# Revit family: 879-002X99-001-DN300-600
name_source: partatom
category: Pipe Accessories
units: mm (PartAtom-declared; Revit-internal decimal feet)

## family parameters
Always vertical = Yes
Cut with Voids When Loaded = No
Part Type = Valve - Breaks Into
Round Connector Dimension = Use Diameter
Shared = No
Work Plane-Based = No

## types (56) — shared parameters
879-0300-00-14400209999 = DN300_PN16
879-0300-00-144002099A0 = DN300_PN16
879-0300-00-14400219999 = DN300_PN16
879-0300-00-144002199A0 = DN300_PN16
879-0300-00-14400229999 = DN300_PN16
879-0300-00-144002299A0 = DN300_PN16
879-0300-00-14400239990 = DN300_PN16
879-0300-00-144002399A0 = DN300_PN16
879-0350-00-14400209999 = DN350_PN16
879-0350-00-144002099A0 = DN350_PN16
879-0350-00-14400219999 = DN350_PN16
879-0350-00-144002199A0 = DN350_PN16
879-0350-00-14400229999 = DN350_PN16
879-0350-00-144002299A0 = DN350_PN16
879-0350-00-14400239999 = DN350_PN16
879-0350-00-144002399A0 = DN350_PN16
879-0400-00-14400209999 = DN400_PN16
879-0400-00-144002099A0 = DN400_PN16
879-0400-00-14400219999 = DN400_PN16
879-0400-00-144002199A0 = DN400_PN16
879-0400-00-14400229999 = DN400_PN16
879-0400-00-144002299A0 = DN400_PN16
879-0400-00-14400239999 = DN400_PN16
879-0400-00-144002399A0 = DN400_PN16
879-0450-00-14400209999 = DN450_PN16
879-0450-00-144002099A0 = DN450_PN16
879-0450-00-14400219999 = DN450_PN16
879-0450-00-144002199A0 = DN450_PN16
879-0450-00-14400229999 = DN450_PN16
879-0450-00-144002299A0 = DN450_PN16
879-0450-00-14400239999 = DN450_PN16
879-0450-00-144002399A0 = DN450_PN16
879-0500-00-14400209999 = DN500_PN16
879-0500-00-144002099A0 = DN500_PN16
879-0500-00-14400219999 = DN500_PN16
879-0500-00-144002199A0 = DN500_PN16
879-0500-00-14400229999 = DN500_PN16
879-0500-00-144002299A0 = DN500_PN16
879-0500-00-14400239990 = DN500_PN16
879-0500-00-144002399A0 = DN500_PN16
879-0600-00-04400209999 = DN600_PN10
879-0600-00-044002099A0 = DN600_PN10
879-0600-00-04400219999 = DN600_PN10
879-0600-00-044002199A0 = DN600_PN10
879-0600-00-04400229999 = DN600_PN10
879-0600-00-044002299A0 = DN600_PN10
879-0600-00-04400239999 = DN600_PN10
879-0600-00-044002399A0 = DN600_PN10
879-0600-00-14400209999 = DN600_PN16
879-0600-00-144002099A0 = DN600_PN16
879-0600-00-14400219999 = DN600_PN16
879-0600-00-144002199A0 = DN600_PN16
879-0600-00-14400229999 = DN600_PN16
879-0600-00-144002299A0 = DN600_PN16
879-0600-00-14400239999 = DN600_PN16
879-0600-00-144002399A0 = DN600_PN16
Body_wall_thickness = 10 mm  [stored 0.0328084 ft]
Description_ = AVK CONSTANT FLOW CONTROL VALVE
Search_Table = 879-002X99-001-DN300-600
URL product pages = https://www.avkvalves.com

## per-type parameters (varying)
- 879-0300-00-14400209999_DN300_PN16: Body_Collar_Dia=88.54 mm; Body_Collar_Dia_2=76.23 mm; Body_Flange_Dia=274.19 mm; Body_Flange_Dia_2=303.57 mm; Body_Height_1=212.5 mm; Body_Height_2=106.25 mm; Body_Height_3=94.5 mm; Body_Height_4=121.25 mm; Body_Top_Dia=38.12 mm; Body_Top_Dia_2=31.76 mm; Body_With_Dia=212.5 mm; Body_With_Dia_2=229.73 mm; Bolt_support=566.67 mm; Bolt_support_2=283.33 mm; Bolt_support_Dia=20 mm  [stored 0.0656168 ft]; Bolt_support_lenght=170 mm; Bolt_support_lenght_2=180 mm; Bottom_profile=75 mm; D1=185 mm; DN=300 mm; FOD=230 mm; Fillet_Length=10 mm  [stored 0.0328084 ft]; Flange_thickness=24.5 mm  [stored 0.0803806 ft]; H3=760 mm; ID=150 mm; L=850 mm; L1=867 mm; L_Ref=858.5 mm; PG_Dia=100 mm; PG_Ref=141.67 mm; PG_depth=14 mm  [stored 0.0459318 ft]; PG_ref=160 mm; Pilot_Dia_1=52.5 mm; Pilot_Dia_2=105 mm; Pilot_Dia_3=35 mm  [stored 0.114829 ft]; Pilot_Dia_4=17.5 mm  [stored 0.0574147 ft]; Pilot_Dia_5=11.67 mm; Pilot_top_1=489.13 mm; Pilot_top_ref=40.88 mm; Profile1_Height=361 mm; Profile1_Length=62.16 mm; Profile1_Length_2=41.44 mm; Profile_Dia=10 mm  [stored 0.0328084 ft]; Profile_Dia_2=10 mm  [stored 0.0328084 ft]; Profile_Dia_3=20 mm  [stored 0.0656168 ft]; Top_Profile=340 mm; Top_Profile_Ref=345 mm; Top_Ref=448.25 mm; Top_Ref_2=468.69 mm; W=555 mm; W_Ref=550 mm
- 879-0300-00-144002099A0_DN300_PN16: Body_Collar_Dia=88.54 mm; Body_Collar_Dia_2=76.23 mm; Body_Flange_Dia=274.19 mm; Body_Flange_Dia_2=303.57 mm; Body_Height_1=212.5 mm; Body_Height_2=106.25 mm; Body_Height_3=106 mm; Body_Height_4=121.25 mm; Body_Top_Dia=38.12 mm; Body_Top_Dia_2=31.76 mm; Body_With_Dia=212.5 mm; Body_With_Dia_2=229.73 mm; Bolt_support=566.67 mm; Bolt_support_2=283.33 mm; Bolt_support_Dia=20 mm  [stored 0.0656168 ft]; Bolt_support_lenght=170.05 mm; Bolt_support_lenght_2=180.05 mm; Bottom_profile=75.03 mm; D1=185 mm; DN=300.1 mm; FOD=230 mm; Fillet_Length=10 mm  [stored 0.0328084 ft]; Flange_thickness=24.5 mm  [stored 0.0803806 ft]; H3=760 mm; ID=150.05 mm; L=850 mm; L1=867 mm; L_Ref=858.5 mm; PG_Dia=100.03 mm; PG_Ref=141.67 mm; PG_depth=14 mm  [stored 0.0459318 ft]; PG_ref=160.05 mm; Pilot_Dia_1=52.5 mm; Pilot_Dia_2=105 mm; Pilot_Dia_3=35 mm  [stored 0.114829 ft]; Pilot_Dia_4=17.5 mm  [stored 0.0574147 ft]; Pilot_Dia_5=11.67 mm; Pilot_top_1=494.88 mm; Pilot_top_ref=35.13 mm; Profile1_Height=400 mm; Profile1_Length=62.16 mm; Profile1_Length_2=41.44 mm; Profile_Dia=10 mm  [stored 0.0328084 ft]; Profile_Dia_2=10 mm  [stored 0.0328084 ft]; Profile_Dia_3=20 mm  [stored 0.0656168 ft]; Top_Profile=340 mm; Top_Profile_Ref=345 mm; Top_Ref=459.75 mm; Top_Ref_2=477.31 mm; W=555 mm; W_Ref=550 mm
- 879-0300-00-14400219999_DN300_PN16: Body_Collar_Dia=88.54 mm; Body_Collar_Dia_2=76.23 mm; Body_Flange_Dia=274.19 mm; Body_Flange_Dia_2=303.57 mm; Body_Height_1=212.5 mm; Body_Height_2=106.25 mm; Body_Height_3=94.5 mm; Body_Height_4=121.25 mm; Body_Top_Dia=38.12 mm; Body_Top_Dia_2=31.76 mm; Body_With_Dia=212.5 mm; Body_With_Dia_2=229.73 mm; Bolt_support=566.67 mm; Bolt_support_2=283.33 mm; Bolt_support_Dia=20 mm  [stored 0.0656168 ft]; Bolt_support_lenght=170.1 mm; Bolt_support_lenght_2=180.1 mm; Bottom_profile=75.05 mm; D1=185 mm; DN=300.2 mm; FOD=230 mm; Fillet_Length=10 mm  [stored 0.0328084 ft]; Flange_thickness=24.5 mm  [stored 0.0803806 ft]; H3=760 mm; ID=150.1 mm; L=850 mm; L1=867 mm; L_Ref=858.5 mm; PG_Dia=100.07 mm; PG_Ref=141.67 mm; PG_depth=14 mm  [stored 0.0459318 ft]; PG_ref=160.1 mm; Pilot_Dia_1=54.5 mm; Pilot_Dia_2=109 mm; Pilot_Dia_3=36.33 mm; Pilot_Dia_4=18.17 mm; Pilot_Dia_5=12.11 mm; Pilot_top_1=489.13 mm; Pilot_top_ref=40.88 mm; Profile1_Height=380 mm; Profile1_Length=62.16 mm; Profile1_Length_2=41.44 mm; Profile_Dia=10 mm  [stored 0.0328084 ft]; Profile_Dia_2=10 mm  [stored 0.0328084 ft]; Profile_Dia_3=20 mm  [stored 0.0656168 ft]; Top_Profile=340 mm; Top_Profile_Ref=345 mm; Top_Ref=448.25 mm; Top_Ref_2=468.69 mm; W=555 mm; W_Ref=550 mm
- 879-0300-00-144002199A0_DN300_PN16: Body_Collar_Dia=88.54 mm; Body_Collar_Dia_2=76.23 mm; Body_Flange_Dia=274.19 mm; Body_Flange_Dia_2=303.57 mm; Body_Height_1=212.5 mm; Body_Height_2=106.25 mm; Body_Height_3=94.5 mm; Body_Height_4=121.25 mm; Body_Top_Dia=38.12 mm; Body_Top_Dia_2=31.76 mm; Body_With_Dia=212.5 mm; Body_With_Dia_2=229.73 mm; Bolt_support=566.67 mm; Bolt_support_2=283.33 mm; Bolt_support_Dia=20 mm  [stored 0.0656168 ft]; Bolt_support_lenght=170.15 mm; Bolt_support_lenght_2=180.15 mm; Bottom_profile=75.08 mm; D1=185 mm; DN=300.3 mm; FOD=230 mm; Fillet_Length=10 mm  [stored 0.0328084 ft]; Flange_thickness=24.5 mm  [stored 0.0803806 ft]; H3=760 mm; ID=150.15 mm; L=850 mm; L1=867 mm; L_Ref=858.5 mm; PG_Dia=100.1 mm; PG_Ref=141.67 mm; PG_depth=14 mm  [stored 0.0459318 ft]; PG_ref=160.15 mm; Pilot_Dia_1=54.5 mm; Pilot_Dia_2=109 mm; Pilot_Dia_3=36.33 mm; Pilot_Dia_4=18.17 mm; Pilot_Dia_5=12.11 mm; Pilot_top_1=489.13 mm; Pilot_top_ref=40.88 mm; Profile1_Height=380 mm; Profile1_Length=62.16 mm; Profile1_Length_2=41.44 mm; Profile_Dia=10 mm  [stored 0.0328084 ft]; Profile_Dia_2=10 mm  [stored 0.0328084 ft]; Profile_Dia_3=20 mm  [stored 0.0656168 ft]; Top_Profile=340 mm; Top_Profile_Ref=345 mm; Top_Ref=448.25 mm; Top_Ref_2=468.69 mm; W=555 mm; W_Ref=550 mm
- 879-0300-00-14400229999_DN300_PN16: Body_Collar_Dia=88.54 mm; Body_Collar_Dia_2=76.23 mm; Body_Flange_Dia=274.19 mm; Body_Flange_Dia_2=303.57 mm; Body_Height_1=212.5 mm; Body_Height_2=106.25 mm; Body_Height_3=94.5 mm; Body_Height_4=121.25 mm; Body_Top_Dia=38.12 mm; Body_Top_Dia_2=31.76 mm; Body_With_Dia=212.5 mm; Body_With_Dia_2=229.73 mm; Bolt_support=566.67 mm; Bolt_support_2=283.33 mm; Bolt_support_Dia=20 mm  [stored 0.0656168 ft]; Bolt_support_lenght=170.2 mm; Bolt_support_lenght_2=180.2 mm; Bottom_profile=75.1 mm; D1=185 mm; DN=300.4 mm; FOD=230 mm; Fillet_Length=10 mm  [stored 0.0328084 ft]; Flange_thickness=24.5 mm  [stored 0.0803806 ft]; H3=760 mm; ID=150.2 mm; L=850 mm; L1=867 mm; L_Ref=858.5 mm; PG_Dia=100.13 mm; PG_Ref=141.67 mm; PG_depth=14 mm  [stored 0.0459318 ft]; PG_ref=160.2 mm; Pilot_Dia_1=52.5 mm; Pilot_Dia_2=105 mm; Pilot_Dia_3=35 mm  [stored 0.114829 ft]; Pilot_Dia_4=17.5 mm  [stored 0.0574147 ft]; Pilot_Dia_5=11.67 mm; Pilot_top_1=489.13 mm; Pilot_top_ref=40.88 mm; Profile1_Height=361 mm; Profile1_Length=62.16 mm; Profile1_Length_2=41.44 mm; Profile_Dia=10 mm  [stored 0.0328084 ft]; Profile_Dia_2=10 mm  [stored 0.0328084 ft]; Profile_Dia_3=20 mm  [stored 0.0656168 ft]; Top_Profile=340 mm; Top_Profile_Ref=345 mm; Top_Ref=448.25 mm; Top_Ref_2=468.69 mm; W=555 mm; W_Ref=550 mm
- 879-0300-00-144002299A0_DN300_PN16: Body_Collar_Dia=88.54 mm; Body_Collar_Dia_2=76.23 mm; Body_Flange_Dia=274.19 mm; Body_Flange_Dia_2=303.57 mm; Body_Height_1=212.5 mm; Body_Height_2=106.25 mm; Body_Height_3=106 mm; Body_Height_4=121.25 mm; Body_Top_Dia=38.12 mm; Body_Top_Dia_2=31.76 mm; Body_With_Dia=212.5 mm; Body_With_Dia_2=229.73 mm; Bolt_support=566.67 mm; Bolt_support_2=283.33 mm; Bolt_support_Dia=20 mm  [stored 0.0656168 ft]; Bolt_support_lenght=170.25 mm; Bolt_support_lenght_2=180.25 mm; Bottom_profile=75.13 mm; D1=185 mm; DN=300.5 mm; FOD=230 mm; Fillet_Length=10 mm  [stored 0.0328084 ft]; Flange_thickness=24.5 mm  [stored 0.0803806 ft]; H3=760 mm; ID=150.25 mm; L=850 mm; L1=867 mm; L_Ref=858.5 mm; PG_Dia=100.17 mm; PG_Ref=141.67 mm; PG_depth=14 mm  [stored 0.0459318 ft]; PG_ref=160.25 mm; Pilot_Dia_1=52.5 mm; Pilot_Dia_2=105 mm; Pilot_Dia_3=35 mm  [stored 0.114829 ft]; Pilot_Dia_4=17.5 mm  [stored 0.0574147 ft]; Pilot_Dia_5=11.67 mm; Pilot_top_1=494.88 mm; Pilot_top_ref=35.13 mm; Profile1_Height=400 mm; Profile1_Length=62.16 mm; Profile1_Length_2=41.44 mm; Profile_Dia=10 mm  [stored 0.0328084 ft]; Profile_Dia_2=10 mm  [stored 0.0328084 ft]; Profile_Dia_3=20 mm  [stored 0.0656168 ft]; Top_Profile=340 mm; Top_Profile_Ref=345 mm; Top_Ref=459.75 mm; Top_Ref_2=477.31 mm; W=555 mm; W_Ref=550 mm
- 879-0300-00-14400239990_DN300_PN16: Body_Collar_Dia=88.54 mm; Body_Collar_Dia_2=76.23 mm; Body_Flange_Dia=274.19 mm; Body_Flange_Dia_2=303.57 mm; Body_Height_1=212.5 mm; Body_Height_2=106.25 mm; Body_Height_3=94.5 mm; Body_Height_4=121.25 mm; Body_Top_Dia=38.12 mm; Body_Top_Dia_2=31.76 mm; Body_With_Dia=212.5 mm; Body_With_Dia_2=229.73 mm; Bolt_support=566.67 mm; Bolt_support_2=283.33 mm; Bolt_support_Dia=20 mm  [stored 0.0656168 ft]; Bolt_support_lenght=170.3 mm; Bolt_support_lenght_2=180.3 mm; Bottom_profile=75.15 mm; D1=185 mm; DN=300.6 mm; FOD=230 mm; Fillet_Length=10 mm  [stored 0.0328084 ft]; Flange_thickness=24.5 mm  [stored 0.0803806 ft]; H3=760 mm; ID=150.3 mm; L=850 mm; L1=867 mm; L_Ref=858.5 mm; PG_Dia=100.2 mm; PG_Ref=141.67 mm; PG_depth=14 mm  [stored 0.0459318 ft]; PG_ref=160.3 mm; Pilot_Dia_1=54.5 mm; Pilot_Dia_2=109 mm; Pilot_Dia_3=36.33 mm; Pilot_Dia_4=18.17 mm; Pilot_Dia_5=12.11 mm; Pilot_top_1=489.13 mm; Pilot_top_ref=40.88 mm; Profile1_Height=380 mm; Profile1_Length=62.16 mm; Profile1_Length_2=41.44 mm; Profile_Dia=10 mm  [stored 0.0328084 ft]; Profile_Dia_2=10 mm  [stored 0.0328084 ft]; Profile_Dia_3=20 mm  [stored 0.0656168 ft]; Top_Profile=340 mm; Top_Profile_Ref=345 mm; Top_Ref=448.25 mm; Top_Ref_2=468.69 mm; W=555 mm; W_Ref=550 mm
- 879-0300-00-144002399A0_DN300_PN16: Body_Collar_Dia=88.54 mm; Body_Collar_Dia_2=76.23 mm; Body_Flange_Dia=274.19 mm; Body_Flange_Dia_2=303.57 mm; Body_Height_1=212.5 mm; Body_Height_2=106.25 mm; Body_Height_3=94.5 mm; Body_Height_4=121.25 mm; Body_Top_Dia=38.12 mm; Body_Top_Dia_2=31.76 mm; Body_With_Dia=212.5 mm; Body_With_Dia_2=229.73 mm; Bolt_support=566.67 mm; Bolt_support_2=283.33 mm; Bolt_support_Dia=20 mm  [stored 0.0656168 ft]; Bolt_support_lenght=170.35 mm; Bolt_support_lenght_2=180.35 mm; Bottom_profile=75.18 mm; D1=185 mm; DN=300.7 mm; FOD=230 mm; Fillet_Length=10 mm  [stored 0.0328084 ft]; Flange_thickness=24.5 mm  [stored 0.0803806 ft]; H3=760 mm; ID=150.35 mm; L=850 mm; L1=867 mm; L_Ref=858.5 mm; PG_Dia=100.23 mm; PG_Ref=141.67 mm; PG_depth=14 mm  [stored 0.0459318 ft]; PG_ref=160.35 mm; Pilot_Dia_1=54.5 mm; Pilot_Dia_2=109 mm; Pilot_Dia_3=36.33 mm; Pilot_Dia_4=18.17 mm; Pilot_Dia_5=12.11 mm; Pilot_top_1=489.13 mm; Pilot_top_ref=40.88 mm; Profile1_Height=380 mm; Profile1_Length=62.16 mm; Profile1_Length_2=41.44 mm; Profile_Dia=10 mm  [stored 0.0328084 ft]; Profile_Dia_2=10 mm  [stored 0.0328084 ft]; Profile_Dia_3=20 mm  [stored 0.0656168 ft]; Top_Profile=340 mm; Top_Profile_Ref=345 mm; Top_Ref=448.25 mm; Top_Ref_2=468.69 mm; W=555 mm; W_Ref=550 mm
- 879-0350-00-14400209999_DN350_PN16: Body_Collar_Dia=102.08 mm; Body_Collar_Dia_2=87.89 mm; Body_Flange_Dia=316.13 mm; Body_Flange_Dia_2=350 mm; Body_Height_1=245 mm; Body_Height_2=122.5 mm; Body_Height_3=98 mm; Body_Height_4=137.5 mm; Body_Top_Dia=43.95 mm; Body_Top_Dia_2=36.62 mm; Body_With_Dia=245 mm; Body_With_Dia_2=264.86 mm; Bolt_support=653.33 mm; Bolt_support_2=326.67 mm; Bolt_support_Dia=30 mm  [stored 0.0984252 ft]; Bolt_support_lenght=195 mm; Bolt_support_lenght_2=205 mm; Bottom_profile=87.5 mm; D1=214.5 mm; DN=350 mm; FOD=260 mm; Fillet_Length=15 mm  [stored 0.0492126 ft]; Flange_thickness=26.5 mm  [stored 0.0869423 ft]; H3=845 mm; ID=175 mm; L=980 mm; L1=997 mm; L_Ref=988.5 mm; PG_Dia=116.67 mm; PG_Ref=163.33 mm; PG_depth=21 mm  [stored 0.0688976 ft]; PG_ref=185 mm; Pilot_Dia_1=60.5 mm; Pilot_Dia_2=121 mm; Pilot_Dia_3=40.33 mm; Pilot_Dia_4=20.17 mm; Pilot_Dia_5=13.44 mm; Pilot_top_1=542.75 mm; Pilot_top_ref=42.25 mm; Profile1_Height=430 mm; Profile1_Length=70.27 mm; Profile1_Length_2=46.85 mm; Profile_Dia=15 mm  [stored 0.0492126 ft]; Profile_Dia_2=15 mm  [stored 0.0492126 ft]; Profile_Dia_3=30 mm  [stored 0.0984252 ft]; Top_Profile=392 mm; Top_Profile_Ref=397 mm; Top_Ref=500.5 mm; Top_Ref_2=521.63 mm; W=605 mm; W_Ref=597.5 mm
- 879-0350-00-144002099A0_DN350_PN16: Body_Collar_Dia=102.08 mm; Body_Collar_Dia_2=87.89 mm; Body_Flange_Dia=316.13 mm; Body_Flange_Dia_2=350 mm; Body_Height_1=245 mm; Body_Height_2=122.5 mm; Body_Height_3=98 mm; Body_Height_4=137.5 mm; Body_Top_Dia=43.95 mm; Body_Top_Dia_2=36.62 mm; Body_With_Dia=245 mm; Body_With_Dia_2=264.86 mm; Bolt_support=653.33 mm; Bolt_support_2=326.67 mm; Bolt_support_Dia=30 mm  [stored 0.0984252 ft]; Bolt_support_lenght=195.05 mm; Bolt_support_lenght_2=205.05 mm; Bottom_profile=87.53 mm; D1=214.5 mm; DN=350.1 mm; FOD=260 mm; Fillet_Length=15 mm  [stored 0.0492126 ft]; Flange_thickness=26.5 mm  [stored 0.0869423 ft]; H3=845 mm; ID=175.05 mm; L=980 mm; L1=997 mm; L_Ref=988.5 mm; PG_Dia=116.7 mm; PG_Ref=163.33 mm; PG_depth=21 mm  [stored 0.0688976 ft]; PG_ref=185.05 mm; Pilot_Dia_1=60.5 mm; Pilot_Dia_2=121 mm; Pilot_Dia_3=40.33 mm; Pilot_Dia_4=20.17 mm; Pilot_Dia_5=13.44 mm; Pilot_top_1=542.75 mm; Pilot_top_ref=42.25 mm; Profile1_Height=430 mm; Profile1_Length=70.27 mm; Profile1_Length_2=46.85 mm; Profile_Dia=15 mm  [stored 0.0492126 ft]; Profile_Dia_2=15 mm  [stored 0.0492126 ft]; Profile_Dia_3=30 mm  [stored 0.0984252 ft]; Top_Profile=392 mm; Top_Profile_Ref=397 mm; Top_Ref=500.5 mm; Top_Ref_2=521.63 mm; W=605 mm; W_Ref=597.5 mm
- 879-0350-00-14400219999_DN350_PN16: Body_Collar_Dia=102.08 mm; Body_Collar_Dia_2=87.89 mm; Body_Flange_Dia=316.13 mm; Body_Flange_Dia_2=350 mm; Body_Height_1=245 mm; Body_Height_2=122.5 mm; Body_Height_3=89 mm; Body_Height_4=137.5 mm; Body_Top_Dia=43.95 mm; Body_Top_Dia_2=36.62 mm; Body_With_Dia=245 mm; Body_With_Dia_2=264.86 mm; Bolt_support=653.33 mm; Bolt_support_2=326.67 mm; Bolt_support_Dia=30 mm  [stored 0.0984252 ft]; Bolt_support_lenght=195.1 mm; Bolt_support_lenght_2=205.1 mm; Bottom_profile=87.55 mm; D1=214.5 mm; DN=350.2 mm; FOD=260 mm; Fillet_Length=15 mm  [stored 0.0492126 ft]; Flange_thickness=26.5 mm  [stored 0.0869423 ft]; H3=845 mm; ID=175.1 mm; L=980 mm; L1=997 mm; L_Ref=988.5 mm; PG_Dia=116.73 mm; PG_Ref=163.33 mm; PG_depth=21 mm  [stored 0.0688976 ft]; PG_ref=185.1 mm; Pilot_Dia_1=63 mm; Pilot_Dia_2=126 mm; Pilot_Dia_3=42 mm; Pilot_Dia_4=21 mm  [stored 0.0688976 ft]; Pilot_Dia_5=14 mm  [stored 0.0459318 ft]; Pilot_top_1=538.25 mm; Pilot_top_ref=46.75 mm; Profile1_Height=430 mm; Profile1_Length=70.27 mm; Profile1_Length_2=46.85 mm; Profile_Dia=15 mm  [stored 0.0492126 ft]; Profile_Dia_2=15 mm  [stored 0.0492126 ft]; Profile_Dia_3=30 mm  [stored 0.0984252 ft]; Top_Profile=392 mm; Top_Profile_Ref=397 mm; Top_Ref=491.5 mm; Top_Ref_2=514.88 mm; W=605 mm; W_Ref=597.5 mm
- 879-0350-00-144002199A0_DN350_PN16: Body_Collar_Dia=102.08 mm; Body_Collar_Dia_2=87.89 mm; Body_Flange_Dia=316.13 mm; Body_Flange_Dia_2=350 mm; Body_Height_1=245 mm; Body_Height_2=122.5 mm; Body_Height_3=89 mm; Body_Height_4=137.5 mm; Body_Top_Dia=43.95 mm; Body_Top_Dia_2=36.62 mm; Body_With_Dia=245 mm; Body_With_Dia_2=264.86 mm; Bolt_support=653.33 mm; Bolt_support_2=326.67 mm; Bolt_support_Dia=30 mm  [stored 0.0984252 ft]; Bolt_support_lenght=195.15 mm; Bolt_support_lenght_2=205.15 mm; Bottom_profile=87.58 mm; D1=214.5 mm; DN=350.3 mm; FOD=260 mm; Fillet_Length=15 mm  [stored 0.0492126 ft]; Flange_thickness=26.5 mm  [stored 0.0869423 ft]; H3=845 mm; ID=175.15 mm; L=980 mm; L1=997 mm; L_Ref=988.5 mm; PG_Dia=116.77 mm; PG_Ref=163.33 mm; PG_depth=21 mm  [stored 0.0688976 ft]; PG_ref=185.15 mm; Pilot_Dia_1=63 mm; Pilot_Dia_2=126 mm; Pilot_Dia_3=42 mm; Pilot_Dia_4=21 mm  [stored 0.0688976 ft]; Pilot_Dia_5=14 mm  [stored 0.0459318 ft]; Pilot_top_1=538.25 mm; Pilot_top_ref=46.75 mm; Profile1_Height=430 mm; Profile1_Length=70.27 mm; Profile1_Length_2=46.85 mm; Profile_Dia=15 mm  [stored 0.0492126 ft]; Profile_Dia_2=15 mm  [stored 0.0492126 ft]; Profile_Dia_3=30 mm  [stored 0.0984252 ft]; Top_Profile=392 mm; Top_Profile_Ref=397 mm; Top_Ref=491.5 mm; Top_Ref_2=514.88 mm; W=605 mm; W_Ref=597.5 mm
- 879-0350-00-14400229999_DN350_PN16: Body_Collar_Dia=102.08 mm; Body_Collar_Dia_2=87.89 mm; Body_Flange_Dia=316.13 mm; Body_Flange_Dia_2=350 mm; Body_Height_1=245 mm; Body_Height_2=122.5 mm; Body_Height_3=98 mm; Body_Height_4=137.5 mm; Body_Top_Dia=43.95 mm; Body_Top_Dia_2=36.62 mm; Body_With_Dia=245 mm; Body_With_Dia_2=264.86 mm; Bolt_support=653.33 mm; Bolt_support_2=326.67 mm; Bolt_support_Dia=30 mm  [stored 0.0984252 ft]; Bolt_support_lenght=195.2 mm; Bolt_support_lenght_2=205.2 mm; Bottom_profile=87.6 mm; D1=214.5 mm; DN=350.4 mm; FOD=260 mm; Fillet_Length=15 mm  [stored 0.0492126 ft]; Flange_thickness=26.5 mm  [stored 0.0869423 ft]; H3=845 mm; ID=175.2 mm; L=980 mm; L1=997 mm; L_Ref=988.5 mm; PG_Dia=116.8 mm; PG_Ref=163.33 mm; PG_depth=21 mm  [stored 0.0688976 ft]; PG_ref=185.2 mm; Pilot_Dia_1=60.5 mm; Pilot_Dia_2=121 mm; Pilot_Dia_3=40.33 mm; Pilot_Dia_4=20.17 mm; Pilot_Dia_5=13.44 mm; Pilot_top_1=542.75 mm; Pilot_top_ref=42.25 mm; Profile1_Height=430 mm; Profile1_Length=70.27 mm; Profile1_Length_2=46.85 mm; Profile_Dia=15 mm  [stored 0.0492126 ft]; Profile_Dia_2=15 mm  [stored 0.0492126 ft]; Profile_Dia_3=30 mm  [stored 0.0984252 ft]; Top_Profile=392 mm; Top_Profile_Ref=397 mm; Top_Ref=500.5 mm; Top_Ref_2=521.63 mm; W=605 mm; W_Ref=597.5 mm
- 879-0350-00-144002299A0_DN350_PN16: Body_Collar_Dia=102.08 mm; Body_Collar_Dia_2=87.89 mm; Body_Flange_Dia=316.13 mm; Body_Flange_Dia_2=350 mm; Body_Height_1=245 mm; Body_Height_2=122.5 mm; Body_Height_3=98 mm; Body_Height_4=137.5 mm; Body_Top_Dia=43.95 mm; Body_Top_Dia_2=36.62 mm; Body_With_Dia=245 mm; Body_With_Dia_2=264.86 mm; Bolt_support=653.33 mm; Bolt_support_2=326.67 mm; Bolt_support_Dia=30 mm  [stored 0.0984252 ft]; Bolt_support_lenght=195.25 mm; Bolt_support_lenght_2=205.25 mm; Bottom_profile=87.63 mm; D1=214.5 mm; DN=350.5 mm; FOD=260 mm; Fillet_Length=15 mm  [stored 0.0492126 ft]; Flange_thickness=26.5 mm  [stored 0.0869423 ft]; H3=845 mm; ID=175.25 mm; L=980 mm; L1=997 mm; L_Ref=988.5 mm; PG_Dia=116.83 mm; PG_Ref=163.33 mm; PG_depth=21 mm  [stored 0.0688976 ft]; PG_ref=185.25 mm; Pilot_Dia_1=60.5 mm; Pilot_Dia_2=121 mm; Pilot_Dia_3=40.33 mm; Pilot_Dia_4=20.17 mm; Pilot_Dia_5=13.44 mm; Pilot_top_1=542.75 mm; Pilot_top_ref=42.25 mm; Profile1_Height=430 mm; Profile1_Length=70.27 mm; Profile1_Length_2=46.85 mm; Profile_Dia=15 mm  [stored 0.0492126 ft]; Profile_Dia_2=15 mm  [stored 0.0492126 ft]; Profile_Dia_3=30 mm  [stored 0.0984252 ft]; Top_Profile=392 mm; Top_Profile_Ref=397 mm; Top_Ref=500.5 mm; Top_Ref_2=521.63 mm; W=605 mm; W_Ref=597.5 mm
- 879-0350-00-14400239999_DN350_PN16: Body_Collar_Dia=102.08 mm; Body_Collar_Dia_2=87.89 mm; Body_Flange_Dia=316.13 mm; Body_Flange_Dia_2=350 mm; Body_Height_1=245 mm; Body_Height_2=122.5 mm; Body_Height_3=89 mm; Body_Height_4=137.5 mm; Body_Top_Dia=43.95 mm; Body_Top_Dia_2=36.62 mm; Body_With_Dia=245 mm; Body_With_Dia_2=264.86 mm; Bolt_support=653.33 mm; Bolt_support_2=326.67 mm; Bolt_support_Dia=30 mm  [stored 0.0984252 ft]; Bolt_support_lenght=195.3 mm; Bolt_support_lenght_2=205.3 mm; Bottom_profile=87.65 mm; D1=214.5 mm; DN=350.6 mm; FOD=260 mm; Fillet_Length=15 mm  [stored 0.0492126 ft]; Flange_thickness=26.5 mm  [stored 0.0869423 ft]; H3=845 mm; ID=175.3 mm; L=980 mm; L1=997 mm; L_Ref=988.5 mm; PG_Dia=116.87 mm; PG_Ref=163.33 mm; PG_depth=21 mm  [stored 0.0688976 ft]; PG_ref=185.3 mm; Pilot_Dia_1=63 mm; Pilot_Dia_2=126 mm; Pilot_Dia_3=42 mm; Pilot_Dia_4=21 mm  [stored 0.0688976 ft]; Pilot_Dia_5=14 mm  [stored 0.0459318 ft]; Pilot_top_1=538.25 mm; Pilot_top_ref=46.75 mm; Profile1_Height=430 mm; Profile1_Length=70.27 mm; Profile1_Length_2=46.85 mm; Profile_Dia=15 mm  [stored 0.0492126 ft]; Profile_Dia_2=15 mm  [stored 0.0492126 ft]; Profile_Dia_3=30 mm  [stored 0.0984252 ft]; Top_Profile=392 mm; Top_Profile_Ref=397 mm; Top_Ref=491.5 mm; Top_Ref_2=514.88 mm; W=605 mm; W_Ref=597.5 mm
- 879-0350-00-144002399A0_DN350_PN16: Body_Collar_Dia=102.08 mm; Body_Collar_Dia_2=87.89 mm; Body_Flange_Dia=316.13 mm; Body_Flange_Dia_2=350 mm; Body_Height_1=245 mm; Body_Height_2=122.5 mm; Body_Height_3=89 mm; Body_Height_4=137.5 mm; Body_Top_Dia=43.95 mm; Body_Top_Dia_2=36.62 mm; Body_With_Dia=245 mm; Body_With_Dia_2=264.86 mm; Bolt_support=653.33 mm; Bolt_support_2=326.67 mm; Bolt_support_Dia=30 mm  [stored 0.0984252 ft]; Bolt_support_lenght=195.35 mm; Bolt_support_lenght_2=205.35 mm; Bottom_profile=87.68 mm; D1=214.5 mm; DN=350.7 mm; FOD=260 mm; Fillet_Length=15 mm  [stored 0.0492126 ft]; Flange_thickness=26.5 mm  [stored 0.0869423 ft]; H3=845 mm; ID=175.35 mm; L=980 mm; L1=997 mm; L_Ref=988.5 mm; PG_Dia=116.9 mm; PG_Ref=163.33 mm; PG_depth=21 mm  [stored 0.0688976 ft]; PG_ref=185.35 mm; Pilot_Dia_1=63 mm; Pilot_Dia_2=126 mm; Pilot_Dia_3=42 mm; Pilot_Dia_4=21 mm  [stored 0.0688976 ft]; Pilot_Dia_5=14 mm  [stored 0.0459318 ft]; Pilot_top_1=538.25 mm; Pilot_top_ref=46.75 mm; Profile1_Height=430 mm; Profile1_Length=70.27 mm; Profile1_Length_2=46.85 mm; Profile_Dia=15 mm  [stored 0.0492126 ft]; Profile_Dia_2=15 mm  [stored 0.0492126 ft]; Profile_Dia_3=30 mm  [stored 0.0984252 ft]; Top_Profile=392 mm; Top_Profile_Ref=397 mm; Top_Ref=491.5 mm; Top_Ref_2=514.88 mm; W=605 mm; W_Ref=597.5 mm
- 879-0400-00-14400209999_DN400_PN16: Body_Collar_Dia=114.58 mm; Body_Collar_Dia_2=98.65 mm; Body_Flange_Dia=354.84 mm; Body_Flange_Dia_2=392.86 mm; Body_Height_1=275 mm; Body_Height_2=137.5 mm; Body_Height_3=110 mm; Body_Height_4=152.5 mm; Body_Top_Dia=49.33 mm; Body_Top_Dia_2=41.11 mm; Body_With_Dia=275 mm; Body_With_Dia_2=297.3 mm; Bolt_support=733.33 mm; Bolt_support_2=366.67 mm; Bolt_support_Dia=30 mm  [stored 0.0984252 ft]; Bolt_support_lenght=220 mm; Bolt_support_lenght_2=230 mm; Bottom_profile=100 mm; D1=240 mm; DN=400 mm; FOD=290 mm; Fillet_Length=20 mm  [stored 0.0656168 ft]; Flange_thickness=28 mm  [stored 0.0918635 ft]; H3=970 mm; ID=200 mm; L=1100 mm; L1=1117 mm; L_Ref=1108.5 mm; PG_Dia=133.33 mm; PG_Ref=183.33 mm; PG_depth=21 mm  [stored 0.0688976 ft]; PG_ref=210 mm; Pilot_Dia_1=69 mm; Pilot_Dia_2=138 mm; Pilot_Dia_3=46 mm; Pilot_Dia_4=23 mm  [stored 0.0754593 ft]; Pilot_Dia_5=15.33 mm; Pilot_top_1=618.75 mm; Pilot_top_ref=61.25 mm; Profile1_Height=480 mm; Profile1_Length=78.38 mm; Profile1_Length_2=52.25 mm; Profile_Dia=15 mm  [stored 0.0492126 ft]; Profile_Dia_2=15 mm  [stored 0.0492126 ft]; Profile_Dia_3=30 mm  [stored 0.0984252 ft]; Top_Profile=440 mm; Top_Profile_Ref=445 mm; Top_Ref=557.5 mm; Top_Ref_2=588.13 mm; W=710 mm; W_Ref=702.5 mm
- 879-0400-00-144002099A0_DN400_PN16: Body_Collar_Dia=114.58 mm; Body_Collar_Dia_2=98.65 mm; Body_Flange_Dia=354.84 mm; Body_Flange_Dia_2=392.86 mm; Body_Height_1=275 mm; Body_Height_2=137.5 mm; Body_Height_3=122 mm; Body_Height_4=152.5 mm; Body_Top_Dia=49.33 mm; Body_Top_Dia_2=41.11 mm; Body_With_Dia=275 mm; Body_With_Dia_2=297.3 mm; Bolt_support=733.33 mm; Bolt_support_2=366.67 mm; Bolt_support_Dia=30 mm  [stored 0.0984252 ft]; Bolt_support_lenght=220.05 mm; Bolt_support_lenght_2=230.05 mm; Bottom_profile=100.03 mm; D1=240 mm; DN=400.1 mm; FOD=290 mm; Fillet_Length=20 mm  [stored 0.0656168 ft]; Flange_thickness=28 mm  [stored 0.0918635 ft]; H3=970 mm; ID=200.05 mm; L=1100 mm; L1=1117 mm; L_Ref=1108.5 mm; PG_Dia=133.37 mm; PG_Ref=183.33 mm; PG_depth=21 mm  [stored 0.0688976 ft]; PG_ref=210.05 mm; Pilot_Dia_1=69 mm; Pilot_Dia_2=138 mm; Pilot_Dia_3=46 mm; Pilot_Dia_4=23 mm  [stored 0.0754593 ft]; Pilot_Dia_5=15.33 mm; Pilot_top_1=624.75 mm; Pilot_top_ref=55.25 mm; Profile1_Height=480 mm; Profile1_Length=78.38 mm; Profile1_Length_2=52.25 mm; Profile_Dia=15 mm  [stored 0.0492126 ft]; Profile_Dia_2=15 mm  [stored 0.0492126 ft]; Profile_Dia_3=30 mm  [stored 0.0984252 ft]; Top_Profile=440 mm; Top_Profile_Ref=445 mm; Top_Ref=569.5 mm; Top_Ref_2=597.13 mm; W=710 mm; W_Ref=702.5 mm
- 879-0400-00-14400219999_DN400_PN16: Body_Collar_Dia=114.58 mm; Body_Collar_Dia_2=98.65 mm; Body_Flange_Dia=354.84 mm; Body_Flange_Dia_2=392.86 mm; Body_Height_1=275 mm; Body_Height_2=137.5 mm; Body_Height_3=100 mm; Body_Height_4=152.5 mm; Body_Top_Dia=49.33 mm; Body_Top_Dia_2=41.11 mm; Body_With_Dia=275 mm; Body_With_Dia_2=297.3 mm; Bolt_support=733.33 mm; Bolt_support_2=366.67 mm; Bolt_support_Dia=30 mm  [stored 0.0984252 ft]; Bolt_support_lenght=220.1 mm; Bolt_support_lenght_2=230.1 mm; Bottom_profile=100.05 mm; D1=240 mm; DN=400.2 mm; FOD=290 mm; Fillet_Length=20 mm  [stored 0.0656168 ft]; Flange_thickness=28 mm  [stored 0.0918635 ft]; H3=970 mm; ID=200.1 mm; L=1100 mm; L1=1117 mm; L_Ref=1108.5 mm; PG_Dia=133.4 mm; PG_Ref=183.33 mm; PG_depth=21 mm  [stored 0.0688976 ft]; PG_ref=210.1 mm; Pilot_Dia_1=71 mm; Pilot_Dia_2=142 mm; Pilot_Dia_3=47.33 mm; Pilot_Dia_4=23.67 mm; Pilot_Dia_5=15.78 mm; Pilot_top_1=613.75 mm; Pilot_top_ref=66.25 mm; Profile1_Height=480 mm; Profile1_Length=78.38 mm; Profile1_Length_2=52.25 mm; Profile_Dia=15 mm  [stored 0.0492126 ft]; Profile_Dia_2=15 mm  [stored 0.0492126 ft]; Profile_Dia_3=30 mm  [stored 0.0984252 ft]; Top_Profile=440 mm; Top_Profile_Ref=445 mm; Top_Ref=547.5 mm; Top_Ref_2=580.63 mm; W=710 mm; W_Ref=702.5 mm
- 879-0400-00-144002199A0_DN400_PN16: Body_Collar_Dia=114.58 mm; Body_Collar_Dia_2=98.65 mm; Body_Flange_Dia=354.84 mm; Body_Flange_Dia_2=392.86 mm; Body_Height_1=275 mm; Body_Height_2=137.5 mm; Body_Height_3=110 mm; Body_Height_4=152.5 mm; Body_Top_Dia=49.33 mm; Body_Top_Dia_2=41.11 mm; Body_With_Dia=275 mm; Body_With_Dia_2=297.3 mm; Bolt_support=733.33 mm; Bolt_support_2=366.67 mm; Bolt_support_Dia=30 mm  [stored 0.0984252 ft]; Bolt_support_lenght=220.15 mm; Bolt_support_lenght_2=230.15 mm; Bottom_profile=100.08 mm; D1=240 mm; DN=400.3 mm; FOD=290 mm; Fillet_Length=20 mm  [stored 0.0656168 ft]; Flange_thickness=28 mm  [stored 0.0918635 ft]; H3=970 mm; ID=200.15 mm; L=1100 mm; L1=1117 mm; L_Ref=1108.5 mm; PG_Dia=133.43 mm; PG_Ref=183.33 mm; PG_depth=21 mm  [stored 0.0688976 ft]; PG_ref=210.15 mm; Pilot_Dia_1=71 mm; Pilot_Dia_2=142 mm; Pilot_Dia_3=47.33 mm; Pilot_Dia_4=23.67 mm; Pilot_Dia_5=15.78 mm; Pilot_top_1=618.75 mm; Pilot_top_ref=61.25 mm; Profile1_Height=480 mm; Profile1_Length=78.38 mm; Profile1_Length_2=52.25 mm; Profile_Dia=15 mm  [stored 0.0492126 ft]; Profile_Dia_2=15 mm  [stored 0.0492126 ft]; Profile_Dia_3=30 mm  [stored 0.0984252 ft]; Top_Profile=440 mm; Top_Profile_Ref=445 mm; Top_Ref=557.5 mm; Top_Ref_2=588.13 mm; W=710 mm; W_Ref=702.5 mm
- 879-0400-00-14400229999_DN400_PN16: Body_Collar_Dia=114.58 mm; Body_Collar_Dia_2=98.65 mm; Body_Flange_Dia=354.84 mm; Body_Flange_Dia_2=392.86 mm; Body_Height_1=275 mm; Body_Height_2=137.5 mm; Body_Height_3=110 mm; Body_Height_4=152.5 mm; Body_Top_Dia=49.33 mm; Body_Top_Dia_2=41.11 mm; Body_With_Dia=275 mm; Body_With_Dia_2=297.3 mm; Bolt_support=733.33 mm; Bolt_support_2=366.67 mm; Bolt_support_Dia=30 mm  [stored 0.0984252 ft]; Bolt_support_lenght=220.2 mm; Bolt_support_lenght_2=230.2 mm; Bottom_profile=100.1 mm; D1=240 mm; DN=400.4 mm; FOD=290 mm; Fillet_Length=20 mm  [stored 0.0656168 ft]; Flange_thickness=28 mm  [stored 0.0918635 ft]; H3=970 mm; ID=200.2 mm; L=1100 mm; L1=1117 mm; L_Ref=1108.5 mm; PG_Dia=133.47 mm; PG_Ref=183.33 mm; PG_depth=21 mm  [stored 0.0688976 ft]; PG_ref=210.2 mm; Pilot_Dia_1=69 mm; Pilot_Dia_2=138 mm; Pilot_Dia_3=46 mm; Pilot_Dia_4=23 mm  [stored 0.0754593 ft]; Pilot_Dia_5=15.33 mm; Pilot_top_1=618.75 mm; Pilot_top_ref=61.25 mm; Profile1_Height=480 mm; Profile1_Length=78.38 mm; Profile1_Length_2=52.25 mm; Profile_Dia=15 mm  [stored 0.0492126 ft]; Profile_Dia_2=15 mm  [stored 0.0492126 ft]; Profile_Dia_3=30 mm  [stored 0.0984252 ft]; Top_Profile=440 mm; Top_Profile_Ref=445 mm; Top_Ref=557.5 mm; Top_Ref_2=588.13 mm; W=710 mm; W_Ref=702.5 mm
- 879-0400-00-144002299A0_DN400_PN16: Body_Collar_Dia=114.58 mm; Body_Collar_Dia_2=98.65 mm; Body_Flange_Dia=354.84 mm; Body_Flange_Dia_2=392.86 mm; Body_Height_1=275 mm; Body_Height_2=137.5 mm; Body_Height_3=122 mm; Body_Height_4=152.5 mm; Body_Top_Dia=49.33 mm; Body_Top_Dia_2=41.11 mm; Body_With_Dia=275 mm; Body_With_Dia_2=297.3 mm; Bolt_support=733.33 mm; Bolt_support_2=366.67 mm; Bolt_support_Dia=30 mm  [stored 0.0984252 ft]; Bolt_support_lenght=220.25 mm; Bolt_support_lenght_2=230.25 mm; Bottom_profile=100.13 mm; D1=240 mm; DN=400.5 mm; FOD=290 mm; Fillet_Length=20 mm  [stored 0.0656168 ft]; Flange_thickness=28 mm  [stored 0.0918635 ft]; H3=970 mm; ID=200.25 mm; L=1100 mm; L1=1117 mm; L_Ref=1108.5 mm; PG_Dia=133.5 mm; PG_Ref=183.33 mm; PG_depth=21 mm  [stored 0.0688976 ft]; PG_ref=210.25 mm; Pilot_Dia_1=69 mm; Pilot_Dia_2=138 mm; Pilot_Dia_3=46 mm; Pilot_Dia_4=23 mm  [stored 0.0754593 ft]; Pilot_Dia_5=15.33 mm; Pilot_top_1=624.75 mm; Pilot_top_ref=55.25 mm; Profile1_Height=480 mm; Profile1_Length=78.38 mm; Profile1_Length_2=52.25 mm; Profile_Dia=15 mm  [stored 0.0492126 ft]; Profile_Dia_2=15 mm  [stored 0.0492126 ft]; Profile_Dia_3=30 mm  [stored 0.0984252 ft]; Top_Profile=440 mm; Top_Profile_Ref=445 mm; Top_Ref=569.5 mm; Top_Ref_2=597.13 mm; W=710 mm; W_Ref=702.5 mm
- 879-0400-00-14400239999_DN400_PN16: Body_Collar_Dia=114.58 mm; Body_Collar_Dia_2=98.65 mm; Body_Flange_Dia=354.84 mm; Body_Flange_Dia_2=392.86 mm; Body_Height_1=275 mm; Body_Height_2=137.5 mm; Body_Height_3=100 mm; Body_Height_4=152.5 mm; Body_Top_Dia=49.33 mm; Body_Top_Dia_2=41.11 mm; Body_With_Dia=275 mm; Body_With_Dia_2=297.3 mm; Bolt_support=733.33 mm; Bolt_support_2=366.67 mm; Bolt_support_Dia=30 mm  [stored 0.0984252 ft]; Bolt_support_lenght=220.3 mm; Bolt_support_lenght_2=230.3 mm; Bottom_profile=100.15 mm; D1=240 mm; DN=400.6 mm; FOD=290 mm; Fillet_Length=20 mm  [stored 0.0656168 ft]; Flange_thickness=28 mm  [stored 0.0918635 ft]; H3=970 mm; ID=200.3 mm; L=1100 mm; L1=1117 mm; L_Ref=1108.5 mm; PG_Dia=133.53 mm; PG_Ref=183.33 mm; PG_depth=21 mm  [stored 0.0688976 ft]; PG_ref=210.3 mm; Pilot_Dia_1=71 mm; Pilot_Dia_2=142 mm; Pilot_Dia_3=47.33 mm; Pilot_Dia_4=23.67 mm; Pilot_Dia_5=15.78 mm; Pilot_top_1=613.75 mm; Pilot_top_ref=66.25 mm; Profile1_Height=480 mm; Profile1_Length=78.38 mm; Profile1_Length_2=52.25 mm; Profile_Dia=15 mm  [stored 0.0492126 ft]; Profile_Dia_2=15 mm  [stored 0.0492126 ft]; Profile_Dia_3=30 mm  [stored 0.0984252 ft]; Top_Profile=440 mm; Top_Profile_Ref=445 mm; Top_Ref=547.5 mm; Top_Ref_2=580.63 mm; W=710 mm; W_Ref=702.5 mm
- 879-0400-00-144002399A0_DN400_PN16: Body_Collar_Dia=114.58 mm; Body_Collar_Dia_2=98.65 mm; Body_Flange_Dia=354.84 mm; Body_Flange_Dia_2=392.86 mm; Body_Height_1=275 mm; Body_Height_2=137.5 mm; Body_Height_3=110 mm; Body_Height_4=152.5 mm; Body_Top_Dia=49.33 mm; Body_Top_Dia_2=41.11 mm; Body_With_Dia=275 mm; Body_With_Dia_2=297.3 mm; Bolt_support=733.33 mm; Bolt_support_2=366.67 mm; Bolt_support_Dia=30 mm  [stored 0.0984252 ft]; Bolt_support_lenght=220.35 mm; Bolt_support_lenght_2=230.35 mm; Bottom_profile=100.18 mm; D1=240 mm; DN=400.7 mm; FOD=290 mm; Fillet_Length=20 mm  [stored 0.0656168 ft]; Flange_thickness=28 mm  [stored 0.0918635 ft]; H3=970 mm; ID=200.35 mm; L=1100 mm; L1=1117 mm; L_Ref=1108.5 mm; PG_Dia=133.57 mm; PG_Ref=183.33 mm; PG_depth=21 mm  [stored 0.0688976 ft]; PG_ref=210.35 mm; Pilot_Dia_1=71 mm; Pilot_Dia_2=142 mm; Pilot_Dia_3=47.33 mm; Pilot_Dia_4=23.67 mm; Pilot_Dia_5=15.78 mm; Pilot_top_1=618.75 mm; Pilot_top_ref=61.25 mm; Profile1_Height=480 mm; Profile1_Length=78.38 mm; Profile1_Length_2=52.25 mm; Profile_Dia=15 mm  [stored 0.0492126 ft]; Profile_Dia_2=15 mm  [stored 0.0492126 ft]; Profile_Dia_3=30 mm  [stored 0.0984252 ft]; Top_Profile=440 mm; Top_Profile_Ref=445 mm; Top_Ref=557.5 mm; Top_Ref_2=588.13 mm; W=710 mm; W_Ref=702.5 mm
- 879-0450-00-14400209999_DN450_PN16: Body_Collar_Dia=125 mm; Body_Collar_Dia_2=107.62 mm; Body_Flange_Dia=387.1 mm; Body_Flange_Dia_2=428.57 mm; Body_Height_1=300 mm; Body_Height_2=150 mm; Body_Height_3=120 mm; Body_Height_4=165 mm; Body_Top_Dia=53.81 mm; Body_Top_Dia_2=44.84 mm; Body_With_Dia=300 mm; Body_With_Dia_2=324.32 mm; Bolt_support=800 mm; Bolt_support_2=400 mm; Bolt_support_Dia=30 mm  [stored 0.0984252 ft]; Bolt_support_lenght=245 mm; Bolt_support_lenght_2=255 mm; Bottom_profile=112.5 mm; D1=274 mm; DN=450 mm; FOD=320 mm; Fillet_Length=20 mm  [stored 0.0656168 ft]; Flange_thickness=30 mm  [stored 0.0984252 ft]; H3=1030 mm; ID=225 mm; L=1200 mm; L1=1217 mm; L_Ref=1208.5 mm; PG_Dia=150 mm; PG_Ref=200 mm; PG_depth=21 mm  [stored 0.0688976 ft]; PG_ref=235 mm; Pilot_Dia_1=75.5 mm; Pilot_Dia_2=151 mm; Pilot_Dia_3=50.33 mm; Pilot_Dia_4=25.17 mm; Pilot_Dia_5=16.78 mm; Pilot_top_1=657.5 mm; Pilot_top_ref=52.5 mm; Profile1_Height=509 mm; Profile1_Length=86.49 mm; Profile1_Length_2=57.66 mm; Profile_Dia=15 mm  [stored 0.0492126 ft]; Profile_Dia_2=15 mm  [stored 0.0492126 ft]; Profile_Dia_3=30 mm  [stored 0.0984252 ft]; Top_Profile=480 mm; Top_Profile_Ref=485 mm; Top_Ref=605 mm; Top_Ref_2=631.25 mm; W=780 mm; W_Ref=772.5 mm
- 879-0450-00-144002099A0_DN450_PN16: Body_Collar_Dia=125 mm; Body_Collar_Dia_2=107.62 mm; Body_Flange_Dia=387.1 mm; Body_Flange_Dia_2=428.57 mm; Body_Height_1=300 mm; Body_Height_2=150 mm; Body_Height_3=120 mm; Body_Height_4=165 mm; Body_Top_Dia=53.81 mm; Body_Top_Dia_2=44.84 mm; Body_With_Dia=300 mm; Body_With_Dia_2=324.32 mm; Bolt_support=800 mm; Bolt_support_2=400 mm; Bolt_support_Dia=30 mm  [stored 0.0984252 ft]; Bolt_support_lenght=245.05 mm; Bolt_support_lenght_2=255.05 mm; Bottom_profile=112.53 mm; D1=274 mm; DN=450.1 mm; FOD=320 mm; Fillet_Length=20 mm  [stored 0.0656168 ft]; Flange_thickness=30 mm  [stored 0.0984252 ft]; H3=1030 mm; ID=225.05 mm; L=1200 mm; L1=1217 mm; L_Ref=1208.5 mm; PG_Dia=150.03 mm; PG_Ref=200 mm; PG_depth=21 mm  [stored 0.0688976 ft]; PG_ref=235.05 mm; Pilot_Dia_1=75.5 mm; Pilot_Dia_2=151 mm; Pilot_Dia_3=50.33 mm; Pilot_Dia_4=25.17 mm; Pilot_Dia_5=16.78 mm; Pilot_top_1=657.5 mm; Pilot_top_ref=52.5 mm; Profile1_Height=530.5 mm; Profile1_Length=86.49 mm; Profile1_Length_2=57.66 mm; Profile_Dia=15 mm  [stored 0.0492126 ft]; Profile_Dia_2=15 mm  [stored 0.0492126 ft]; Profile_Dia_3=30 mm  [stored 0.0984252 ft]; Top_Profile=480 mm; Top_Profile_Ref=485 mm; Top_Ref=605 mm; Top_Ref_2=631.25 mm; W=780 mm; W_Ref=772.5 mm
- 879-0450-00-14400219999_DN450_PN16: Body_Collar_Dia=125 mm; Body_Collar_Dia_2=107.62 mm; Body_Flange_Dia=387.1 mm; Body_Flange_Dia_2=428.57 mm; Body_Height_1=300 mm; Body_Height_2=150 mm; Body_Height_3=120 mm; Body_Height_4=165 mm; Body_Top_Dia=53.81 mm; Body_Top_Dia_2=44.84 mm; Body_With_Dia=300 mm; Body_With_Dia_2=324.32 mm; Bolt_support=800 mm; Bolt_support_2=400 mm; Bolt_support_Dia=30 mm  [stored 0.0984252 ft]; Bolt_support_lenght=245.1 mm; Bolt_support_lenght_2=255.1 mm; Bottom_profile=112.55 mm; D1=274 mm; DN=450.2 mm; FOD=320 mm; Fillet_Length=20 mm  [stored 0.0656168 ft]; Flange_thickness=30 mm  [stored 0.0984252 ft]; H3=1030 mm; ID=225.1 mm; L=1200 mm; L1=1217 mm; L_Ref=1208.5 mm; PG_Dia=150.07 mm; PG_Ref=200 mm; PG_depth=21 mm  [stored 0.0688976 ft]; PG_ref=235.1 mm; Pilot_Dia_1=79 mm; Pilot_Dia_2=158 mm; Pilot_Dia_3=52.67 mm; Pilot_Dia_4=26.33 mm; Pilot_Dia_5=17.56 mm; Pilot_top_1=657.5 mm; Pilot_top_ref=52.5 mm; Profile1_Height=530 mm; Profile1_Length=86.49 mm; Profile1_Length_2=57.66 mm; Profile_Dia=15 mm  [stored 0.0492126 ft]; Profile_Dia_2=15 mm  [stored 0.0492126 ft]; Profile_Dia_3=30 mm  [stored 0.0984252 ft]; Top_Profile=480 mm; Top_Profile_Ref=485 mm; Top_Ref=605 mm; Top_Ref_2=631.25 mm; W=780 mm; W_Ref=772.5 mm
- 879-0450-00-144002199A0_DN450_PN16: Body_Collar_Dia=125 mm; Body_Collar_Dia_2=107.62 mm; Body_Flange_Dia=387.1 mm; Body_Flange_Dia_2=428.57 mm; Body_Height_1=300 mm; Body_Height_2=150 mm; Body_Height_3=120 mm; Body_Height_4=165 mm; Body_Top_Dia=53.81 mm; Body_Top_Dia_2=44.84 mm; Body_With_Dia=300 mm; Body_With_Dia_2=324.32 mm; Bolt_support=800 mm; Bolt_support_2=400 mm; Bolt_support_Dia=30 mm  [stored 0.0984252 ft]; Bolt_support_lenght=245.15 mm; Bolt_support_lenght_2=255.15 mm; Bottom_profile=112.58 mm; D1=274 mm; DN=450.3 mm; FOD=320 mm; Fillet_Length=20 mm  [stored 0.0656168 ft]; Flange_thickness=30 mm  [stored 0.0984252 ft]; H3=1030 mm; ID=225.15 mm; L=1200 mm; L1=1217 mm; L_Ref=1208.5 mm; PG_Dia=150.1 mm; PG_Ref=200 mm; PG_depth=21 mm  [stored 0.0688976 ft]; PG_ref=235.15 mm; Pilot_Dia_1=79 mm; Pilot_Dia_2=158 mm; Pilot_Dia_3=52.67 mm; Pilot_Dia_4=26.33 mm; Pilot_Dia_5=17.56 mm; Pilot_top_1=657.5 mm; Pilot_top_ref=52.5 mm; Profile1_Height=530.5 mm; Profile1_Length=86.49 mm; Profile1_Length_2=57.66 mm; Profile_Dia=15 mm  [stored 0.0492126 ft]; Profile_Dia_2=15 mm  [stored 0.0492126 ft]; Profile_Dia_3=30 mm  [stored 0.0984252 ft]; Top_Profile=480 mm; Top_Profile_Ref=485 mm; Top_Ref=605 mm; Top_Ref_2=631.25 mm; W=780 mm; W_Ref=772.5 mm
- 879-0450-00-14400229999_DN450_PN16: Body_Collar_Dia=125 mm; Body_Collar_Dia_2=107.62 mm; Body_Flange_Dia=387.1 mm; Body_Flange_Dia_2=428.57 mm; Body_Height_1=300 mm; Body_Height_2=150 mm; Body_Height_3=120 mm; Body_Height_4=165 mm; Body_Top_Dia=53.81 mm; Body_Top_Dia_2=44.84 mm; Body_With_Dia=300 mm; Body_With_Dia_2=324.32 mm; Bolt_support=800 mm; Bolt_support_2=400 mm; Bolt_support_Dia=30 mm  [stored 0.0984252 ft]; Bolt_support_lenght=245.2 mm; Bolt_support_lenght_2=255.2 mm; Bottom_profile=112.6 mm; D1=274 mm; DN=450.4 mm; FOD=320 mm; Fillet_Length=20 mm  [stored 0.0656168 ft]; Flange_thickness=30 mm  [stored 0.0984252 ft]; H3=1030 mm; ID=225.2 mm; L=1200 mm; L1=1217 mm; L_Ref=1208.5 mm; PG_Dia=150.13 mm; PG_Ref=200 mm; PG_depth=21 mm  [stored 0.0688976 ft]; PG_ref=235.2 mm; Pilot_Dia_1=75.5 mm; Pilot_Dia_2=151 mm; Pilot_Dia_3=50.33 mm; Pilot_Dia_4=25.17 mm; Pilot_Dia_5=16.78 mm; Pilot_top_1=657.5 mm; Pilot_top_ref=52.5 mm; Profile1_Height=509 mm; Profile1_Length=86.49 mm; Profile1_Length_2=57.66 mm; Profile_Dia=15 mm  [stored 0.0492126 ft]; Profile_Dia_2=15 mm  [stored 0.0492126 ft]; Profile_Dia_3=30 mm  [stored 0.0984252 ft]; Top_Profile=480 mm; Top_Profile_Ref=485 mm; Top_Ref=605 mm; Top_Ref_2=631.25 mm; W=780 mm; W_Ref=772.5 mm
- 879-0450-00-144002299A0_DN450_PN16: Body_Collar_Dia=125 mm; Body_Collar_Dia_2=107.62 mm; Body_Flange_Dia=387.1 mm; Body_Flange_Dia_2=428.57 mm; Body_Height_1=300 mm; Body_Height_2=150 mm; Body_Height_3=120 mm; Body_Height_4=165 mm; Body_Top_Dia=53.81 mm; Body_Top_Dia_2=44.84 mm; Body_With_Dia=300 mm; Body_With_Dia_2=324.32 mm; Bolt_support=800 mm; Bolt_support_2=400 mm; Bolt_support_Dia=30 mm  [stored 0.0984252 ft]; Bolt_support_lenght=245.25 mm; Bolt_support_lenght_2=255.25 mm; Bottom_profile=112.63 mm; D1=274 mm; DN=450.5 mm; FOD=320 mm; Fillet_Length=20 mm  [stored 0.0656168 ft]; Flange_thickness=30 mm  [stored 0.0984252 ft]; H3=1030 mm; ID=225.25 mm; L=1200 mm; L1=1217 mm; L_Ref=1208.5 mm; PG_Dia=150.17 mm; PG_Ref=200 mm; PG_depth=21 mm  [stored 0.0688976 ft]; PG_ref=235.25 mm; Pilot_Dia_1=75.5 mm; Pilot_Dia_2=151 mm; Pilot_Dia_3=50.33 mm; Pilot_Dia_4=25.17 mm; Pilot_Dia_5=16.78 mm; Pilot_top_1=657.5 mm; Pilot_top_ref=52.5 mm; Profile1_Height=530.5 mm; Profile1_Length=86.49 mm; Profile1_Length_2=57.66 mm; Profile_Dia=15 mm  [stored 0.0492126 ft]; Profile_Dia_2=15 mm  [stored 0.0492126 ft]; Profile_Dia_3=30 mm  [stored 0.0984252 ft]; Top_Profile=480 mm; Top_Profile_Ref=485 mm; Top_Ref=605 mm; Top_Ref_2=631.25 mm; W=780 mm; W_Ref=772.5 mm
- 879-0450-00-14400239999_DN450_PN16: Body_Collar_Dia=125 mm; Body_Collar_Dia_2=107.62 mm; Body_Flange_Dia=387.1 mm; Body_Flange_Dia_2=428.57 mm; Body_Height_1=300 mm; Body_Height_2=150 mm; Body_Height_3=120 mm; Body_Height_4=165 mm; Body_Top_Dia=53.81 mm; Body_Top_Dia_2=44.84 mm; Body_With_Dia=300 mm; Body_With_Dia_2=324.32 mm; Bolt_support=800 mm; Bolt_support_2=400 mm; Bolt_support_Dia=30 mm  [stored 0.0984252 ft]; Bolt_support_lenght=245.3 mm; Bolt_support_lenght_2=255.3 mm; Bottom_profile=112.65 mm; D1=274 mm; DN=450.6 mm; FOD=320 mm; Fillet_Length=20 mm  [stored 0.0656168 ft]; Flange_thickness=30 mm  [stored 0.0984252 ft]; H3=1030 mm; ID=225.3 mm; L=1200 mm; L1=1217 mm; L_Ref=1208.5 mm; PG_Dia=150.2 mm; PG_Ref=200 mm; PG_depth=21 mm  [stored 0.0688976 ft]; PG_ref=235.3 mm; Pilot_Dia_1=79 mm; Pilot_Dia_2=158 mm; Pilot_Dia_3=52.67 mm; Pilot_Dia_4=26.33 mm; Pilot_Dia_5=17.56 mm; Pilot_top_1=657.5 mm; Pilot_top_ref=52.5 mm; Profile1_Height=530 mm; Profile1_Length=86.49 mm; Profile1_Length_2=57.66 mm; Profile_Dia=15 mm  [stored 0.0492126 ft]; Profile_Dia_2=15 mm  [stored 0.0492126 ft]; Profile_Dia_3=30 mm  [stored 0.0984252 ft]; Top_Profile=480 mm; Top_Profile_Ref=485 mm; Top_Ref=605 mm; Top_Ref_2=631.25 mm; W=780 mm; W_Ref=772.5 mm
- 879-0450-00-144002399A0_DN450_PN16: Body_Collar_Dia=125 mm; Body_Collar_Dia_2=107.62 mm; Body_Flange_Dia=387.1 mm; Body_Flange_Dia_2=428.57 mm; Body_Height_1=300 mm; Body_Height_2=150 mm; Body_Height_3=120 mm; Body_Height_4=165 mm; Body_Top_Dia=53.81 mm; Body_Top_Dia_2=44.84 mm; Body_With_Dia=300 mm; Body_With_Dia_2=324.32 mm; Bolt_support=800 mm; Bolt_support_2=400 mm; Bolt_support_Dia=30 mm  [stored 0.0984252 ft]; Bolt_support_lenght=245.35 mm; Bolt_support_lenght_2=255.35 mm; Bottom_profile=112.68 mm; D1=274 mm; DN=450.7 mm; FOD=320 mm; Fillet_Length=20 mm  [stored 0.0656168 ft]; Flange_thickness=30 mm  [stored 0.0984252 ft]; H3=1030 mm; ID=225.35 mm; L=1200 mm; L1=1217 mm; L_Ref=1208.5 mm; PG_Dia=150.23 mm; PG_Ref=200 mm; PG_depth=21 mm  [stored 0.0688976 ft]; PG_ref=235.35 mm; Pilot_Dia_1=79 mm; Pilot_Dia_2=158 mm; Pilot_Dia_3=52.67 mm; Pilot_Dia_4=26.33 mm; Pilot_Dia_5=17.56 mm; Pilot_top_1=657.5 mm; Pilot_top_ref=52.5 mm; Profile1_Height=530.5 mm; Profile1_Length=86.49 mm; Profile1_Length_2=57.66 mm; Profile_Dia=15 mm  [stored 0.0492126 ft]; Profile_Dia_2=15 mm  [stored 0.0492126 ft]; Profile_Dia_3=30 mm  [stored 0.0984252 ft]; Top_Profile=480 mm; Top_Profile_Ref=485 mm; Top_Ref=605 mm; Top_Ref_2=631.25 mm; W=780 mm; W_Ref=772.5 mm
- 879-0500-00-14400209999_DN500_PN16: Body_Collar_Dia=130.21 mm; Body_Collar_Dia_2=112.11 mm; Body_Flange_Dia=403.23 mm; Body_Flange_Dia_2=446.43 mm; Body_Height_1=312.5 mm; Body_Height_2=156.25 mm; Body_Height_3=125 mm; Body_Height_4=171.25 mm; Body_Top_Dia=56.05 mm; Body_Top_Dia_2=46.71 mm; Body_With_Dia=312.5 mm; Body_With_Dia_2=337.84 mm; Bolt_support=833.33 mm; Bolt_support_2=416.67 mm; Bolt_support_Dia=30 mm  [stored 0.0984252 ft]; Bolt_support_lenght=270 mm; Bolt_support_lenght_2=280 mm; Bottom_profile=125 mm; D1=304.5 mm; DN=500 mm; FOD=357.5 mm; Fillet_Length=25 mm  [stored 0.082021 ft]; Flange_thickness=31.5 mm  [stored 0.103346 ft]; H3=1215 mm; ID=250 mm; L=1250 mm; L1=1267 mm; L_Ref=1258.5 mm; PG_Dia=166.67 mm; PG_Ref=208.33 mm; PG_depth=21 mm  [stored 0.0688976 ft]; PG_ref=260 mm; Pilot_Dia_1=83 mm; Pilot_Dia_2=166 mm; Pilot_Dia_3=55.33 mm; Pilot_Dia_4=27.67 mm; Pilot_Dia_5=18.44 mm; Pilot_top_1=743.13 mm; Pilot_top_ref=114.38 mm; Profile1_Height=541 mm; Profile1_Length=96.62 mm; Profile1_Length_2=64.41 mm; Profile_Dia=15 mm  [stored 0.0492126 ft]; Profile_Dia_2=15 mm  [stored 0.0492126 ft]; Profile_Dia_3=30 mm  [stored 0.0984252 ft]; Top_Profile=500 mm; Top_Profile_Ref=505 mm; Top_Ref=628.75 mm; Top_Ref_2=685.94 mm; W=930 mm; W_Ref=922.5 mm
- 879-0500-00-144002099A0_DN500_PN16: Body_Collar_Dia=130.21 mm; Body_Collar_Dia_2=112.11 mm; Body_Flange_Dia=403.23 mm; Body_Flange_Dia_2=446.43 mm; Body_Height_1=312.5 mm; Body_Height_2=156.25 mm; Body_Height_3=125 mm; Body_Height_4=171.25 mm; Body_Top_Dia=56.05 mm; Body_Top_Dia_2=46.71 mm; Body_With_Dia=312.5 mm; Body_With_Dia_2=337.84 mm; Bolt_support=833.33 mm; Bolt_support_2=416.67 mm; Bolt_support_Dia=30 mm  [stored 0.0984252 ft]; Bolt_support_lenght=270.05 mm; Bolt_support_lenght_2=280.05 mm; Bottom_profile=125.03 mm; D1=304.5 mm; DN=500.1 mm; FOD=357.5 mm; Fillet_Length=25 mm  [stored 0.082021 ft]; Flange_thickness=31.5 mm  [stored 0.103346 ft]; H3=1215 mm; ID=250.05 mm; L=1250 mm; L1=1267 mm; L_Ref=1258.5 mm; PG_Dia=166.7 mm; PG_Ref=208.33 mm; PG_depth=21 mm  [stored 0.0688976 ft]; PG_ref=260.05 mm; Pilot_Dia_1=83 mm; Pilot_Dia_2=166 mm; Pilot_Dia_3=55.33 mm; Pilot_Dia_4=27.67 mm; Pilot_Dia_5=18.44 mm; Pilot_top_1=743.13 mm; Pilot_top_ref=114.38 mm; Profile1_Height=541 mm; Profile1_Length=96.62 mm; Profile1_Length_2=64.41 mm; Profile_Dia=15 mm  [stored 0.0492126 ft]; Profile_Dia_2=15 mm  [stored 0.0492126 ft]; Profile_Dia_3=30 mm  [stored 0.0984252 ft]; Top_Profile=500 mm; Top_Profile_Ref=505 mm; Top_Ref=628.75 mm; Top_Ref_2=685.94 mm; W=930 mm; W_Ref=922.5 mm
- 879-0500-00-14400219999_DN500_PN16: Body_Collar_Dia=130.21 mm; Body_Collar_Dia_2=112.11 mm; Body_Flange_Dia=403.23 mm; Body_Flange_Dia_2=446.43 mm; Body_Height_1=312.5 mm; Body_Height_2=156.25 mm; Body_Height_3=125 mm; Body_Height_4=171.25 mm; Body_Top_Dia=56.05 mm; Body_Top_Dia_2=46.71 mm; Body_With_Dia=312.5 mm; Body_With_Dia_2=337.84 mm; Bolt_support=833.33 mm; Bolt_support_2=416.67 mm; Bolt_support_Dia=30 mm  [stored 0.0984252 ft]; Bolt_support_lenght=270.1 mm; Bolt_support_lenght_2=280.1 mm; Bottom_profile=125.05 mm; D1=304.5 mm; DN=500.2 mm; FOD=357.5 mm; Fillet_Length=25 mm  [stored 0.082021 ft]; Flange_thickness=31.5 mm  [stored 0.103346 ft]; H3=1215 mm; ID=250.1 mm; L=1250 mm; L1=1267 mm; L_Ref=1258.5 mm; PG_Dia=166.73 mm; PG_Ref=208.33 mm; PG_depth=21 mm  [stored 0.0688976 ft]; PG_ref=260.1 mm; Pilot_Dia_1=89 mm; Pilot_Dia_2=178 mm; Pilot_Dia_3=59.33 mm; Pilot_Dia_4=29.67 mm; Pilot_Dia_5=19.78 mm; Pilot_top_1=743.13 mm; Pilot_top_ref=114.38 mm; Profile1_Height=541 mm; Profile1_Length=96.62 mm; Profile1_Length_2=64.41 mm; Profile_Dia=15 mm  [stored 0.0492126 ft]; Profile_Dia_2=15 mm  [stored 0.0492126 ft]; Profile_Dia_3=30 mm  [stored 0.0984252 ft]; Top_Profile=500 mm; Top_Profile_Ref=505 mm; Top_Ref=628.75 mm; Top_Ref_2=685.94 mm; W=930 mm; W_Ref=922.5 mm
- 879-0500-00-144002199A0_DN500_PN16: Body_Collar_Dia=130.21 mm; Body_Collar_Dia_2=112.11 mm; Body_Flange_Dia=403.23 mm; Body_Flange_Dia_2=446.43 mm; Body_Height_1=312.5 mm; Body_Height_2=156.25 mm; Body_Height_3=125 mm; Body_Height_4=171.25 mm; Body_Top_Dia=56.05 mm; Body_Top_Dia_2=46.71 mm; Body_With_Dia=312.5 mm; Body_With_Dia_2=337.84 mm; Bolt_support=833.33 mm; Bolt_support_2=416.67 mm; Bolt_support_Dia=30 mm  [stored 0.0984252 ft]; Bolt_support_lenght=270.15 mm; Bolt_support_lenght_2=280.15 mm; Bottom_profile=125.08 mm; D1=304.5 mm; DN=500.3 mm; FOD=357.5 mm; Fillet_Length=25 mm  [stored 0.082021 ft]; Flange_thickness=31.5 mm  [stored 0.103346 ft]; H3=1215 mm; ID=250.15 mm; L=1250 mm; L1=1267 mm; L_Ref=1258.5 mm; PG_Dia=166.77 mm; PG_Ref=208.33 mm; PG_depth=21 mm  [stored 0.0688976 ft]; PG_ref=260.15 mm; Pilot_Dia_1=89 mm; Pilot_Dia_2=178 mm; Pilot_Dia_3=59.33 mm; Pilot_Dia_4=29.67 mm; Pilot_Dia_5=19.78 mm; Pilot_top_1=743.13 mm; Pilot_top_ref=114.38 mm; Profile1_Height=563 mm; Profile1_Length=96.62 mm; Profile1_Length_2=64.41 mm; Profile_Dia=15 mm  [stored 0.0492126 ft]; Profile_Dia_2=15 mm  [stored 0.0492126 ft]; Profile_Dia_3=30 mm  [stored 0.0984252 ft]; Top_Profile=500 mm; Top_Profile_Ref=505 mm; Top_Ref=628.75 mm; Top_Ref_2=685.94 mm; W=930 mm; W_Ref=922.5 mm
- 879-0500-00-14400229999_DN500_PN16: Body_Collar_Dia=130.21 mm; Body_Collar_Dia_2=112.11 mm; Body_Flange_Dia=403.23 mm; Body_Flange_Dia_2=446.43 mm; Body_Height_1=312.5 mm; Body_Height_2=156.25 mm; Body_Height_3=125 mm; Body_Height_4=171.25 mm; Body_Top_Dia=56.05 mm; Body_Top_Dia_2=46.71 mm; Body_With_Dia=312.5 mm; Body_With_Dia_2=337.84 mm; Bolt_support=833.33 mm; Bolt_support_2=416.67 mm; Bolt_support_Dia=30 mm  [stored 0.0984252 ft]; Bolt_support_lenght=270.2 mm; Bolt_support_lenght_2=280.2 mm; Bottom_profile=125.1 mm; D1=304.5 mm; DN=500.4 mm; FOD=357.5 mm; Fillet_Length=25 mm  [stored 0.082021 ft]; Flange_thickness=31.5 mm  [stored 0.103346 ft]; H3=1215 mm; ID=250.2 mm; L=1250 mm; L1=1267 mm; L_Ref=1258.5 mm; PG_Dia=166.8 mm; PG_Ref=208.33 mm; PG_depth=21 mm  [stored 0.0688976 ft]; PG_ref=260.2 mm; Pilot_Dia_1=83 mm; Pilot_Dia_2=166 mm; Pilot_Dia_3=55.33 mm; Pilot_Dia_4=27.67 mm; Pilot_Dia_5=18.44 mm; Pilot_top_1=743.13 mm; Pilot_top_ref=114.38 mm; Profile1_Height=541 mm; Profile1_Length=96.62 mm; Profile1_Length_2=64.41 mm; Profile_Dia=15 mm  [stored 0.0492126 ft]; Profile_Dia_2=15 mm  [stored 0.0492126 ft]; Profile_Dia_3=30 mm  [stored 0.0984252 ft]; Top_Profile=500 mm; Top_Profile_Ref=505 mm; Top_Ref=628.75 mm; Top_Ref_2=685.94 mm; W=930 mm; W_Ref=922.5 mm
- 879-0500-00-144002299A0_DN500_PN16: Body_Collar_Dia=130.21 mm; Body_Collar_Dia_2=112.11 mm; Body_Flange_Dia=403.23 mm; Body_Flange_Dia_2=446.43 mm; Body_Height_1=312.5 mm; Body_Height_2=156.25 mm; Body_Height_3=125 mm; Body_Height_4=171.25 mm; Body_Top_Dia=56.05 mm; Body_Top_Dia_2=46.71 mm; Body_With_Dia=312.5 mm; Body_With_Dia_2=337.84 mm; Bolt_support=833.33 mm; Bolt_support_2=416.67 mm; Bolt_support_Dia=30 mm  [stored 0.0984252 ft]; Bolt_support_lenght=270.25 mm; Bolt_support_lenght_2=280.25 mm; Bottom_profile=125.13 mm; D1=304.5 mm; DN=500.5 mm; FOD=357.5 mm; Fillet_Length=25 mm  [stored 0.082021 ft]; Flange_thickness=31.5 mm  [stored 0.103346 ft]; H3=1215 mm; ID=250.25 mm; L=1250 mm; L1=1267 mm; L_Ref=1258.5 mm; PG_Dia=166.83 mm; PG_Ref=208.33 mm; PG_depth=21 mm  [stored 0.0688976 ft]; PG_ref=260.25 mm; Pilot_Dia_1=83 mm; Pilot_Dia_2=166 mm; Pilot_Dia_3=55.33 mm; Pilot_Dia_4=27.67 mm; Pilot_Dia_5=18.44 mm; Pilot_top_1=743.13 mm; Pilot_top_ref=114.38 mm; Profile1_Height=541 mm; Profile1_Length=96.62 mm; Profile1_Length_2=64.41 mm; Profile_Dia=15 mm  [stored 0.0492126 ft]; Profile_Dia_2=15 mm  [stored 0.0492126 ft]; Profile_Dia_3=30 mm  [stored 0.0984252 ft]; Top_Profile=500 mm; Top_Profile_Ref=505 mm; Top_Ref=628.75 mm; Top_Ref_2=685.94 mm; W=930 mm; W_Ref=922.5 mm
- 879-0500-00-14400239990_DN500_PN16: Body_Collar_Dia=130.21 mm; Body_Collar_Dia_2=112.11 mm; Body_Flange_Dia=403.23 mm; Body_Flange_Dia_2=446.43 mm; Body_Height_1=312.5 mm; Body_Height_2=156.25 mm; Body_Height_3=125 mm; Body_Height_4=171.25 mm; Body_Top_Dia=56.05 mm; Body_Top_Dia_2=46.71 mm; Body_With_Dia=312.5 mm; Body_With_Dia_2=337.84 mm; Bolt_support=833.33 mm; Bolt_support_2=416.67 mm; Bolt_support_Dia=30 mm  [stored 0.0984252 ft]; Bolt_support_lenght=270.3 mm; Bolt_support_lenght_2=280.3 mm; Bottom_profile=125.15 mm; D1=304.5 mm; DN=500.6 mm; FOD=357.5 mm; Fillet_Length=25 mm  [stored 0.082021 ft]; Flange_thickness=31.5 mm  [stored 0.103346 ft]; H3=1215 mm; ID=250.3 mm; L=1250 mm; L1=1267 mm; L_Ref=1258.5 mm; PG_Dia=166.87 mm; PG_Ref=208.33 mm; PG_depth=21 mm  [stored 0.0688976 ft]; PG_ref=260.3 mm; Pilot_Dia_1=89 mm; Pilot_Dia_2=178 mm; Pilot_Dia_3=59.33 mm; Pilot_Dia_4=29.67 mm; Pilot_Dia_5=19.78 mm; Pilot_top_1=743.13 mm; Pilot_top_ref=114.38 mm; Profile1_Height=541 mm; Profile1_Length=96.62 mm; Profile1_Length_2=64.41 mm; Profile_Dia=15 mm  [stored 0.0492126 ft]; Profile_Dia_2=15 mm  [stored 0.0492126 ft]; Profile_Dia_3=30 mm  [stored 0.0984252 ft]; Top_Profile=500 mm; Top_Profile_Ref=505 mm; Top_Ref=628.75 mm; Top_Ref_2=685.94 mm; W=930 mm; W_Ref=922.5 mm
- 879-0500-00-144002399A0_DN500_PN16: Body_Collar_Dia=130.21 mm; Body_Collar_Dia_2=112.11 mm; Body_Flange_Dia=403.23 mm; Body_Flange_Dia_2=446.43 mm; Body_Height_1=312.5 mm; Body_Height_2=156.25 mm; Body_Height_3=125 mm; Body_Height_4=171.25 mm; Body_Top_Dia=56.05 mm; Body_Top_Dia_2=46.71 mm; Body_With_Dia=312.5 mm; Body_With_Dia_2=337.84 mm; Bolt_support=833.33 mm; Bolt_support_2=416.67 mm; Bolt_support_Dia=30 mm  [stored 0.0984252 ft]; Bolt_support_lenght=270.35 mm; Bolt_support_lenght_2=280.35 mm; Bottom_profile=125.18 mm; D1=304.5 mm; DN=500.7 mm; FOD=357.5 mm; Fillet_Length=25 mm  [stored 0.082021 ft]; Flange_thickness=31.5 mm  [stored 0.103346 ft]; H3=1215 mm; ID=250.35 mm; L=1250 mm; L1=1267 mm; L_Ref=1258.5 mm; PG_Dia=166.9 mm; PG_Ref=208.33 mm; PG_depth=21 mm  [stored 0.0688976 ft]; PG_ref=260.35 mm; Pilot_Dia_1=89 mm; Pilot_Dia_2=178 mm; Pilot_Dia_3=59.33 mm; Pilot_Dia_4=29.67 mm; Pilot_Dia_5=19.78 mm; Pilot_top_1=743.13 mm; Pilot_top_ref=114.38 mm; Profile1_Height=563 mm; Profile1_Length=96.62 mm; Profile1_Length_2=64.41 mm; Profile_Dia=15 mm  [stored 0.0492126 ft]; Profile_Dia_2=15 mm  [stored 0.0492126 ft]; Profile_Dia_3=30 mm  [stored 0.0984252 ft]; Top_Profile=500 mm; Top_Profile_Ref=505 mm; Top_Ref=628.75 mm; Top_Ref_2=685.94 mm; W=930 mm; W_Ref=922.5 mm
- 879-0600-00-04400209999_DN600_PN10: Body_Collar_Dia=151.04 mm; Body_Collar_Dia_2=130.04 mm; Body_Flange_Dia=467.74 mm; Body_Flange_Dia_2=517.86 mm; Body_Height_1=362.5 mm; Body_Height_2=181.25 mm; Body_Height_3=145 mm; Body_Height_4=196.25 mm; Body_Top_Dia=65.02 mm; Body_Top_Dia_2=54.19 mm; Body_With_Dia=362.5 mm; Body_With_Dia_2=391.89 mm; Bolt_support=966.67 mm; Bolt_support_2=483.33 mm; Bolt_support_Dia=30 mm  [stored 0.0984252 ft]; Bolt_support_lenght=320 mm; Bolt_support_lenght_2=330 mm; Bottom_profile=150 mm; D1=341 mm; DN=600 mm; FOD=390 mm; Fillet_Length=30 mm  [stored 0.0984252 ft]; Flange_thickness=36 mm  [stored 0.11811 ft]; H3=1325 mm; ID=300 mm; L=1450 mm; L1=1467 mm; L_Ref=1458.5 mm; PG_Dia=200 mm; PG_Ref=241.67 mm; PG_depth=21 mm  [stored 0.0688976 ft]; PG_ref=310 mm; Pilot_Dia_1=98 mm; Pilot_Dia_2=196 mm; Pilot_Dia_3=65.33 mm; Pilot_Dia_4=32.67 mm; Pilot_Dia_5=21.78 mm; Pilot_top_1=829.38 mm; Pilot_top_ref=105.63 mm; Profile1_Height=616 mm; Profile1_Length=105.41 mm; Profile1_Length_2=70.27 mm; Profile_Dia=15 mm  [stored 0.0492126 ft]; Profile_Dia_2=15 mm  [stored 0.0492126 ft]; Profile_Dia_3=30 mm  [stored 0.0984252 ft]; Top_Profile=580 mm; Top_Profile_Ref=585 mm; Top_Ref=723.75 mm; Top_Ref_2=776.56 mm; W=1020 mm; W_Ref=1012.5 mm
- 879-0600-00-044002099A0_DN600_PN10: Body_Collar_Dia=151.04 mm; Body_Collar_Dia_2=130.04 mm; Body_Flange_Dia=467.74 mm; Body_Flange_Dia_2=517.86 mm; Body_Height_1=362.5 mm; Body_Height_2=181.25 mm; Body_Height_3=145 mm; Body_Height_4=196.25 mm; Body_Top_Dia=65.02 mm; Body_Top_Dia_2=54.19 mm; Body_With_Dia=362.5 mm; Body_With_Dia_2=391.89 mm; Bolt_support=966.67 mm; Bolt_support_2=483.33 mm; Bolt_support_Dia=30 mm  [stored 0.0984252 ft]; Bolt_support_lenght=320.05 mm; Bolt_support_lenght_2=330.05 mm; Bottom_profile=150.03 mm; D1=341 mm; DN=600.1 mm; FOD=390 mm; Fillet_Length=30 mm  [stored 0.0984252 ft]; Flange_thickness=36 mm  [stored 0.11811 ft]; H3=1325 mm; ID=300.05 mm; L=1450 mm; L1=1467 mm; L_Ref=1458.5 mm; PG_Dia=200.03 mm; PG_Ref=241.67 mm; PG_depth=21 mm  [stored 0.0688976 ft]; PG_ref=310.05 mm; Pilot_Dia_1=98 mm; Pilot_Dia_2=196 mm; Pilot_Dia_3=65.33 mm; Pilot_Dia_4=32.67 mm; Pilot_Dia_5=21.78 mm; Pilot_top_1=829.38 mm; Pilot_top_ref=105.63 mm; Profile1_Height=660 mm; Profile1_Length=105.41 mm; Profile1_Length_2=70.27 mm; Profile_Dia=15 mm  [stored 0.0492126 ft]; Profile_Dia_2=15 mm  [stored 0.0492126 ft]; Profile_Dia_3=30 mm  [stored 0.0984252 ft]; Top_Profile=580 mm; Top_Profile_Ref=585 mm; Top_Ref=723.75 mm; Top_Ref_2=776.56 mm; W=1020 mm; W_Ref=1012.5 mm
- 879-0600-00-04400219999_DN600_PN10: Body_Collar_Dia=151.04 mm; Body_Collar_Dia_2=130.04 mm; Body_Flange_Dia=467.74 mm; Body_Flange_Dia_2=517.86 mm; Body_Height_1=362.5 mm; Body_Height_2=181.25 mm; Body_Height_3=145 mm; Body_Height_4=196.25 mm; Body_Top_Dia=65.02 mm; Body_Top_Dia_2=54.19 mm; Body_With_Dia=362.5 mm; Body_With_Dia_2=391.89 mm; Bolt_support=966.67 mm; Bolt_support_2=483.33 mm; Bolt_support_Dia=30 mm  [stored 0.0984252 ft]; Bolt_support_lenght=320.1 mm; Bolt_support_lenght_2=330.1 mm; Bottom_profile=150.05 mm; D1=341 mm; DN=600.2 mm; FOD=390 mm; Fillet_Length=30 mm  [stored 0.0984252 ft]; Flange_thickness=36 mm  [stored 0.11811 ft]; H3=1325 mm; ID=300.1 mm; L=1450 mm; L1=1467 mm; L_Ref=1458.5 mm; PG_Dia=200.07 mm; PG_Ref=241.67 mm; PG_depth=21 mm  [stored 0.0688976 ft]; PG_ref=310.1 mm; Pilot_Dia_1=106 mm; Pilot_Dia_2=212 mm; Pilot_Dia_3=70.67 mm; Pilot_Dia_4=35.33 mm; Pilot_Dia_5=23.56 mm; Pilot_top_1=829.38 mm; Pilot_top_ref=105.63 mm; Profile1_Height=616 mm; Profile1_Length=105.41 mm; Profile1_Length_2=70.27 mm; Profile_Dia=15 mm  [stored 0.0492126 ft]; Profile_Dia_2=15 mm  [stored 0.0492126 ft]; Profile_Dia_3=30 mm  [stored 0.0984252 ft]; Top_Profile=580 mm; Top_Profile_Ref=585 mm; Top_Ref=723.75 mm; Top_Ref_2=776.56 mm; W=1020 mm; W_Ref=1012.5 mm
- 879-0600-00-044002199A0_DN600_PN10: Body_Collar_Dia=151.04 mm; Body_Collar_Dia_2=130.04 mm; Body_Flange_Dia=467.74 mm; Body_Flange_Dia_2=517.86 mm; Body_Height_1=362.5 mm; Body_Height_2=181.25 mm; Body_Height_3=145 mm; Body_Height_4=196.25 mm; Body_Top_Dia=65.02 mm; Body_Top_Dia_2=54.19 mm; Body_With_Dia=362.5 mm; Body_With_Dia_2=391.89 mm; Bolt_support=966.67 mm; Bolt_support_2=483.33 mm; Bolt_support_Dia=30 mm  [stored 0.0984252 ft]; Bolt_support_lenght=320.15 mm; Bolt_support_lenght_2=330.15 mm; Bottom_profile=150.08 mm; D1=341 mm; DN=600.3 mm; FOD=390 mm; Fillet_Length=30 mm  [stored 0.0984252 ft]; Flange_thickness=36 mm  [stored 0.11811 ft]; H3=1325 mm; ID=300.15 mm; L=1450 mm; L1=1467 mm; L_Ref=1458.5 mm; PG_Dia=200.1 mm; PG_Ref=241.67 mm; PG_depth=21 mm  [stored 0.0688976 ft]; PG_ref=310.15 mm; Pilot_Dia_1=106 mm; Pilot_Dia_2=212 mm; Pilot_Dia_3=70.67 mm; Pilot_Dia_4=35.33 mm; Pilot_Dia_5=23.56 mm; Pilot_top_1=829.38 mm; Pilot_top_ref=105.63 mm; Profile1_Height=660 mm; Profile1_Length=105.41 mm; Profile1_Length_2=70.27 mm; Profile_Dia=15 mm  [stored 0.0492126 ft]; Profile_Dia_2=15 mm  [stored 0.0492126 ft]; Profile_Dia_3=30 mm  [stored 0.0984252 ft]; Top_Profile=580 mm; Top_Profile_Ref=585 mm; Top_Ref=723.75 mm; Top_Ref_2=776.56 mm; W=1020 mm; W_Ref=1012.5 mm
- 879-0600-00-04400229999_DN600_PN10: Body_Collar_Dia=151.04 mm; Body_Collar_Dia_2=130.04 mm; Body_Flange_Dia=467.74 mm; Body_Flange_Dia_2=517.86 mm; Body_Height_1=362.5 mm; Body_Height_2=181.25 mm; Body_Height_3=145 mm; Body_Height_4=196.25 mm; Body_Top_Dia=65.02 mm; Body_Top_Dia_2=54.19 mm; Body_With_Dia=362.5 mm; Body_With_Dia_2=391.89 mm; Bolt_support=966.67 mm; Bolt_support_2=483.33 mm; Bolt_support_Dia=30 mm  [stored 0.0984252 ft]; Bolt_support_lenght=320.2 mm; Bolt_support_lenght_2=330.2 mm; Bottom_profile=150.1 mm; D1=341 mm; DN=600.4 mm; FOD=390 mm; Fillet_Length=30 mm  [stored 0.0984252 ft]; Flange_thickness=36 mm  [stored 0.11811 ft]; H3=1325 mm; ID=300.2 mm; L=1450 mm; L1=1467 mm; L_Ref=1458.5 mm; PG_Dia=200.13 mm; PG_Ref=241.67 mm; PG_depth=21 mm  [stored 0.0688976 ft]; PG_ref=310.2 mm; Pilot_Dia_1=98 mm; Pilot_Dia_2=196 mm; Pilot_Dia_3=65.33 mm; Pilot_Dia_4=32.67 mm; Pilot_Dia_5=21.78 mm; Pilot_top_1=829.38 mm; Pilot_top_ref=105.63 mm; Profile1_Height=616 mm; Profile1_Length=105.41 mm; Profile1_Length_2=70.27 mm; Profile_Dia=15 mm  [stored 0.0492126 ft]; Profile_Dia_2=15 mm  [stored 0.0492126 ft]; Profile_Dia_3=30 mm  [stored 0.0984252 ft]; Top_Profile=580 mm; Top_Profile_Ref=585 mm; Top_Ref=723.75 mm; Top_Ref_2=776.56 mm; W=1020 mm; W_Ref=1012.5 mm
- 879-0600-00-044002299A0_DN600_PN10: Body_Collar_Dia=151.04 mm; Body_Collar_Dia_2=130.04 mm; Body_Flange_Dia=467.74 mm; Body_Flange_Dia_2=517.86 mm; Body_Height_1=362.5 mm; Body_Height_2=181.25 mm; Body_Height_3=145 mm; Body_Height_4=196.25 mm; Body_Top_Dia=65.02 mm; Body_Top_Dia_2=54.19 mm; Body_With_Dia=362.5 mm; Body_With_Dia_2=391.89 mm; Bolt_support=966.67 mm; Bolt_support_2=483.33 mm; Bolt_support_Dia=30 mm  [stored 0.0984252 ft]; Bolt_support_lenght=320.25 mm; Bolt_support_lenght_2=330.25 mm; Bottom_profile=150.13 mm; D1=341 mm; DN=600.5 mm; FOD=390 mm; Fillet_Length=30 mm  [stored 0.0984252 ft]; Flange_thickness=36 mm  [stored 0.11811 ft]; H3=1325 mm; ID=300.25 mm; L=1450 mm; L1=1467 mm; L_Ref=1458.5 mm; PG_Dia=200.17 mm; PG_Ref=241.67 mm; PG_depth=21 mm  [stored 0.0688976 ft]; PG_ref=310.25 mm; Pilot_Dia_1=98 mm; Pilot_Dia_2=196 mm; Pilot_Dia_3=65.33 mm; Pilot_Dia_4=32.67 mm; Pilot_Dia_5=21.78 mm; Pilot_top_1=829.38 mm; Pilot_top_ref=105.63 mm; Profile1_Height=660 mm; Profile1_Length=105.41 mm; Profile1_Length_2=70.27 mm; Profile_Dia=15 mm  [stored 0.0492126 ft]; Profile_Dia_2=15 mm  [stored 0.0492126 ft]; Profile_Dia_3=30 mm  [stored 0.0984252 ft]; Top_Profile=580 mm; Top_Profile_Ref=585 mm; Top_Ref=723.75 mm; Top_Ref_2=776.56 mm; W=1020 mm; W_Ref=1012.5 mm
- 879-0600-00-04400239999_DN600_PN10: Body_Collar_Dia=151.04 mm; Body_Collar_Dia_2=130.04 mm; Body_Flange_Dia=467.74 mm; Body_Flange_Dia_2=517.86 mm; Body_Height_1=362.5 mm; Body_Height_2=181.25 mm; Body_Height_3=145 mm; Body_Height_4=196.25 mm; Body_Top_Dia=65.02 mm; Body_Top_Dia_2=54.19 mm; Body_With_Dia=362.5 mm; Body_With_Dia_2=391.89 mm; Bolt_support=966.67 mm; Bolt_support_2=483.33 mm; Bolt_support_Dia=30 mm  [stored 0.0984252 ft]; Bolt_support_lenght=320.3 mm; Bolt_support_lenght_2=330.3 mm; Bottom_profile=150.15 mm; D1=341 mm; DN=600.6 mm; FOD=390 mm; Fillet_Length=30 mm  [stored 0.0984252 ft]; Flange_thickness=36 mm  [stored 0.11811 ft]; H3=1325 mm; ID=300.3 mm; L=1450 mm; L1=1467 mm; L_Ref=1458.5 mm; PG_Dia=200.2 mm; PG_Ref=241.67 mm; PG_depth=21 mm  [stored 0.0688976 ft]; PG_ref=310.3 mm; Pilot_Dia_1=106 mm; Pilot_Dia_2=212 mm; Pilot_Dia_3=70.67 mm; Pilot_Dia_4=35.33 mm; Pilot_Dia_5=23.56 mm; Pilot_top_1=829.38 mm; Pilot_top_ref=105.63 mm; Profile1_Height=616 mm; Profile1_Length=105.41 mm; Profile1_Length_2=70.27 mm; Profile_Dia=15 mm  [stored 0.0492126 ft]; Profile_Dia_2=15 mm  [stored 0.0492126 ft]; Profile_Dia_3=30 mm  [stored 0.0984252 ft]; Top_Profile=580 mm; Top_Profile_Ref=585 mm; Top_Ref=723.75 mm; Top_Ref_2=776.56 mm; W=1020 mm; W_Ref=1012.5 mm
- 879-0600-00-044002399A0_DN600_PN10: Body_Collar_Dia=151.04 mm; Body_Collar_Dia_2=130.04 mm; Body_Flange_Dia=467.74 mm; Body_Flange_Dia_2=517.86 mm; Body_Height_1=362.5 mm; Body_Height_2=181.25 mm; Body_Height_3=145 mm; Body_Height_4=196.25 mm; Body_Top_Dia=65.02 mm; Body_Top_Dia_2=54.19 mm; Body_With_Dia=362.5 mm; Body_With_Dia_2=391.89 mm; Bolt_support=966.67 mm; Bolt_support_2=483.33 mm; Bolt_support_Dia=30 mm  [stored 0.0984252 ft]; Bolt_support_lenght=320.35 mm; Bolt_support_lenght_2=330.35 mm; Bottom_profile=150.18 mm; D1=341 mm; DN=600.7 mm; FOD=390 mm; Fillet_Length=30 mm  [stored 0.0984252 ft]; Flange_thickness=36 mm  [stored 0.11811 ft]; H3=1325 mm; ID=300.35 mm; L=1450 mm; L1=1467 mm; L_Ref=1458.5 mm; PG_Dia=200.23 mm; PG_Ref=241.67 mm; PG_depth=21 mm  [stored 0.0688976 ft]; PG_ref=310.35 mm; Pilot_Dia_1=106 mm; Pilot_Dia_2=212 mm; Pilot_Dia_3=70.67 mm; Pilot_Dia_4=35.33 mm; Pilot_Dia_5=23.56 mm; Pilot_top_1=829.38 mm; Pilot_top_ref=105.63 mm; Profile1_Height=660 mm; Profile1_Length=105.41 mm; Profile1_Length_2=70.27 mm; Profile_Dia=15 mm  [stored 0.0492126 ft]; Profile_Dia_2=15 mm  [stored 0.0492126 ft]; Profile_Dia_3=30 mm  [stored 0.0984252 ft]; Top_Profile=580 mm; Top_Profile_Ref=585 mm; Top_Ref=723.75 mm; Top_Ref_2=776.56 mm; W=1020 mm; W_Ref=1012.5 mm
- 879-0600-00-14400209999_DN600_PN16: Body_Collar_Dia=151.04 mm; Body_Collar_Dia_2=130.04 mm; Body_Flange_Dia=467.74 mm; Body_Flange_Dia_2=517.86 mm; Body_Height_1=362.5 mm; Body_Height_2=181.25 mm; Body_Height_3=145 mm; Body_Height_4=196.25 mm; Body_Top_Dia=65.02 mm; Body_Top_Dia_2=54.19 mm; Body_With_Dia=362.5 mm; Body_With_Dia_2=391.89 mm; Bolt_support=966.67 mm; Bolt_support_2=483.33 mm; Bolt_support_Dia=30 mm  [stored 0.0984252 ft]; Bolt_support_lenght=320.4 mm; Bolt_support_lenght_2=330.4 mm; Bottom_profile=150.2 mm; D1=360 mm; DN=600.8 mm; FOD=420 mm; Fillet_Length=30 mm  [stored 0.0984252 ft]; Flange_thickness=36 mm  [stored 0.11811 ft]; H3=1325 mm; ID=300.4 mm; L=1450 mm; L1=1467 mm; L_Ref=1458.5 mm; PG_Dia=200.27 mm; PG_Ref=241.67 mm; PG_depth=21 mm  [stored 0.0688976 ft]; PG_ref=310.4 mm; Pilot_Dia_1=98 mm; Pilot_Dia_2=196 mm; Pilot_Dia_3=65.33 mm; Pilot_Dia_4=32.67 mm; Pilot_Dia_5=21.78 mm; Pilot_top_1=814.38 mm; Pilot_top_ref=90.63 mm; Profile1_Height=616 mm; Profile1_Length=113.51 mm; Profile1_Length_2=75.68 mm; Profile_Dia=15 mm  [stored 0.0492126 ft]; Profile_Dia_2=15 mm  [stored 0.0492126 ft]; Profile_Dia_3=30 mm  [stored 0.0984252 ft]; Top_Profile=580 mm; Top_Profile_Ref=585 mm; Top_Ref=723.75 mm; Top_Ref_2=769.06 mm; W=1020 mm; W_Ref=1012.5 mm
- 879-0600-00-144002099A0_DN600_PN16: Body_Collar_Dia=151.04 mm; Body_Collar_Dia_2=130.04 mm; Body_Flange_Dia=467.74 mm; Body_Flange_Dia_2=517.86 mm; Body_Height_1=362.5 mm; Body_Height_2=181.25 mm; Body_Height_3=145 mm; Body_Height_4=196.25 mm; Body_Top_Dia=65.02 mm; Body_Top_Dia_2=54.19 mm; Body_With_Dia=362.5 mm; Body_With_Dia_2=391.89 mm; Bolt_support=966.67 mm; Bolt_support_2=483.33 mm; Bolt_support_Dia=30 mm  [stored 0.0984252 ft]; Bolt_support_lenght=320.45 mm; Bolt_support_lenght_2=330.45 mm; Bottom_profile=150.23 mm; D1=360 mm; DN=600.9 mm; FOD=420 mm; Fillet_Length=30 mm  [stored 0.0984252 ft]; Flange_thickness=36 mm  [stored 0.11811 ft]; H3=1325 mm; ID=300.45 mm; L=1450 mm; L1=1467 mm; L_Ref=1458.5 mm; PG_Dia=200.3 mm; PG_Ref=241.67 mm; PG_depth=21 mm  [stored 0.0688976 ft]; PG_ref=310.45 mm; Pilot_Dia_1=98 mm; Pilot_Dia_2=196 mm; Pilot_Dia_3=65.33 mm; Pilot_Dia_4=32.67 mm; Pilot_Dia_5=21.78 mm; Pilot_top_1=814.38 mm; Pilot_top_ref=90.63 mm; Profile1_Height=660 mm; Profile1_Length=113.51 mm; Profile1_Length_2=75.68 mm; Profile_Dia=15 mm  [stored 0.0492126 ft]; Profile_Dia_2=15 mm  [stored 0.0492126 ft]; Profile_Dia_3=30 mm  [stored 0.0984252 ft]; Top_Profile=580 mm; Top_Profile_Ref=585 mm; Top_Ref=723.75 mm; Top_Ref_2=769.06 mm; W=1020 mm; W_Ref=1012.5 mm
- 879-0600-00-14400219999_DN600_PN16: Body_Collar_Dia=151.04 mm; Body_Collar_Dia_2=130.04 mm; Body_Flange_Dia=467.74 mm; Body_Flange_Dia_2=517.86 mm; Body_Height_1=362.5 mm; Body_Height_2=181.25 mm; Body_Height_3=145 mm; Body_Height_4=196.25 mm; Body_Top_Dia=65.02 mm; Body_Top_Dia_2=54.19 mm; Body_With_Dia=362.5 mm; Body_With_Dia_2=391.89 mm; Bolt_support=966.67 mm; Bolt_support_2=483.33 mm; Bolt_support_Dia=30 mm  [stored 0.0984252 ft]; Bolt_support_lenght=320.06 mm; Bolt_support_lenght_2=330.06 mm; Bottom_profile=150.03 mm; D1=360 mm; DN=600.11 mm; FOD=420 mm; Fillet_Length=30 mm  [stored 0.0984252 ft]; Flange_thickness=36 mm  [stored 0.11811 ft]; H3=1325 mm; ID=300.06 mm; L=1450 mm; L1=1467 mm; L_Ref=1458.5 mm; PG_Dia=200.04 mm; PG_Ref=241.67 mm; PG_depth=21 mm  [stored 0.0688976 ft]; PG_ref=310.06 mm; Pilot_Dia_1=106 mm; Pilot_Dia_2=212 mm; Pilot_Dia_3=70.67 mm; Pilot_Dia_4=35.33 mm; Pilot_Dia_5=23.56 mm; Pilot_top_1=814.38 mm; Pilot_top_ref=90.63 mm; Profile1_Height=616 mm; Profile1_Length=113.51 mm; Profile1_Length_2=75.68 mm; Profile_Dia=15 mm  [stored 0.0492126 ft]; Profile_Dia_2=15 mm  [stored 0.0492126 ft]; Profile_Dia_3=30 mm  [stored 0.0984252 ft]; Top_Profile=580 mm; Top_Profile_Ref=585 mm; Top_Ref=723.75 mm; Top_Ref_2=769.06 mm; W=1020 mm; W_Ref=1012.5 mm
- 879-0600-00-144002199A0_DN600_PN16: Body_Collar_Dia=151.04 mm; Body_Collar_Dia_2=130.04 mm; Body_Flange_Dia=467.74 mm; Body_Flange_Dia_2=517.86 mm; Body_Height_1=362.5 mm; Body_Height_2=181.25 mm; Body_Height_3=145 mm; Body_Height_4=196.25 mm; Body_Top_Dia=65.02 mm; Body_Top_Dia_2=54.19 mm; Body_With_Dia=362.5 mm; Body_With_Dia_2=391.89 mm; Bolt_support=966.67 mm; Bolt_support_2=483.33 mm; Bolt_support_Dia=30 mm  [stored 0.0984252 ft]; Bolt_support_lenght=320.06 mm; Bolt_support_lenght_2=330.06 mm; Bottom_profile=150.03 mm; D1=360 mm; DN=600.12 mm; FOD=420 mm; Fillet_Length=30 mm  [stored 0.0984252 ft]; Flange_thickness=36 mm  [stored 0.11811 ft]; H3=1325 mm; ID=300.06 mm; L=1450 mm; L1=1467 mm; L_Ref=1458.5 mm; PG_Dia=200.04 mm; PG_Ref=241.67 mm; PG_depth=21 mm  [stored 0.0688976 ft]; PG_ref=310.06 mm; Pilot_Dia_1=106 mm; Pilot_Dia_2=212 mm; Pilot_Dia_3=70.67 mm; Pilot_Dia_4=35.33 mm; Pilot_Dia_5=23.56 mm; Pilot_top_1=814.38 mm; Pilot_top_ref=90.63 mm; Profile1_Height=660 mm; Profile1_Length=113.51 mm; Profile1_Length_2=75.68 mm; Profile_Dia=15 mm  [stored 0.0492126 ft]; Profile_Dia_2=15 mm  [stored 0.0492126 ft]; Profile_Dia_3=30 mm  [stored 0.0984252 ft]; Top_Profile=580 mm; Top_Profile_Ref=585 mm; Top_Ref=723.75 mm; Top_Ref_2=769.06 mm; W=1020 mm; W_Ref=1012.5 mm
- 879-0600-00-14400229999_DN600_PN16: Body_Collar_Dia=151.04 mm; Body_Collar_Dia_2=130.04 mm; Body_Flange_Dia=467.74 mm; Body_Flange_Dia_2=517.86 mm; Body_Height_1=362.5 mm; Body_Height_2=181.25 mm; Body_Height_3=145 mm; Body_Height_4=196.25 mm; Body_Top_Dia=65.02 mm; Body_Top_Dia_2=54.19 mm; Body_With_Dia=362.5 mm; Body_With_Dia_2=391.89 mm; Bolt_support=966.67 mm; Bolt_support_2=483.33 mm; Bolt_support_Dia=30 mm  [stored 0.0984252 ft]; Bolt_support_lenght=320.07 mm; Bolt_support_lenght_2=330.07 mm; Bottom_profile=150.03 mm; D1=360 mm; DN=600.13 mm; FOD=420 mm; Fillet_Length=30 mm  [stored 0.0984252 ft]; Flange_thickness=36 mm  [stored 0.11811 ft]; H3=1325 mm; ID=300.07 mm; L=1450 mm; L1=1467 mm; L_Ref=1458.5 mm; PG_Dia=200.04 mm; PG_Ref=241.67 mm; PG_depth=21 mm  [stored 0.0688976 ft]; PG_ref=310.07 mm; Pilot_Dia_1=98 mm; Pilot_Dia_2=196 mm; Pilot_Dia_3=65.33 mm; Pilot_Dia_4=32.67 mm; Pilot_Dia_5=21.78 mm; Pilot_top_1=814.38 mm; Pilot_top_ref=90.63 mm; Profile1_Height=616 mm; Profile1_Length=113.51 mm; Profile1_Length_2=75.68 mm; Profile_Dia=15 mm  [stored 0.0492126 ft]; Profile_Dia_2=15 mm  [stored 0.0492126 ft]; Profile_Dia_3=30 mm  [stored 0.0984252 ft]; Top_Profile=580 mm; Top_Profile_Ref=585 mm; Top_Ref=723.75 mm; Top_Ref_2=769.06 mm; W=1020 mm; W_Ref=1012.5 mm
- 879-0600-00-144002299A0_DN600_PN16: Body_Collar_Dia=151.04 mm; Body_Collar_Dia_2=130.04 mm; Body_Flange_Dia=467.74 mm; Body_Flange_Dia_2=517.86 mm; Body_Height_1=362.5 mm; Body_Height_2=181.25 mm; Body_Height_3=145 mm; Body_Height_4=196.25 mm; Body_Top_Dia=65.02 mm; Body_Top_Dia_2=54.19 mm; Body_With_Dia=362.5 mm; Body_With_Dia_2=391.89 mm; Bolt_support=966.67 mm; Bolt_support_2=483.33 mm; Bolt_support_Dia=30 mm  [stored 0.0984252 ft]; Bolt_support_lenght=320.07 mm; Bolt_support_lenght_2=330.07 mm; Bottom_profile=150.04 mm; D1=360 mm; DN=600.14 mm; FOD=420 mm; Fillet_Length=30 mm  [stored 0.0984252 ft]; Flange_thickness=36 mm  [stored 0.11811 ft]; H3=1325 mm; ID=300.07 mm; L=1450 mm; L1=1467 mm; L_Ref=1458.5 mm; PG_Dia=200.05 mm; PG_Ref=241.67 mm; PG_depth=21 mm  [stored 0.0688976 ft]; PG_ref=310.07 mm; Pilot_Dia_1=98 mm; Pilot_Dia_2=196 mm; Pilot_Dia_3=65.33 mm; Pilot_Dia_4=32.67 mm; Pilot_Dia_5=21.78 mm; Pilot_top_1=814.38 mm; Pilot_top_ref=90.63 mm; Profile1_Height=660 mm; Profile1_Length=113.51 mm; Profile1_Length_2=75.68 mm; Profile_Dia=15 mm  [stored 0.0492126 ft]; Profile_Dia_2=15 mm  [stored 0.0492126 ft]; Profile_Dia_3=30 mm  [stored 0.0984252 ft]; Top_Profile=580 mm; Top_Profile_Ref=585 mm; Top_Ref=723.75 mm; Top_Ref_2=769.06 mm; W=1020 mm; W_Ref=1012.5 mm
- 879-0600-00-14400239999_DN600_PN16: Body_Collar_Dia=151.04 mm; Body_Collar_Dia_2=130.04 mm; Body_Flange_Dia=467.74 mm; Body_Flange_Dia_2=517.86 mm; Body_Height_1=362.5 mm; Body_Height_2=181.25 mm; Body_Height_3=145 mm; Body_Height_4=196.25 mm; Body_Top_Dia=65.02 mm; Body_Top_Dia_2=54.19 mm; Body_With_Dia=362.5 mm; Body_With_Dia_2=391.89 mm; Bolt_support=966.67 mm; Bolt_support_2=483.33 mm; Bolt_support_Dia=30 mm  [stored 0.0984252 ft]; Bolt_support_lenght=320.08 mm; Bolt_support_lenght_2=330.08 mm; Bottom_profile=150.04 mm; D1=360 mm; DN=600.15 mm; FOD=420 mm; Fillet_Length=30 mm  [stored 0.0984252 ft]; Flange_thickness=36 mm  [stored 0.11811 ft]; H3=1325 mm; ID=300.08 mm; L=1450 mm; L1=1467 mm; L_Ref=1458.5 mm; PG_Dia=200.05 mm; PG_Ref=241.67 mm; PG_depth=21 mm  [stored 0.0688976 ft]; PG_ref=310.08 mm; Pilot_Dia_1=106 mm; Pilot_Dia_2=212 mm; Pilot_Dia_3=70.67 mm; Pilot_Dia_4=35.33 mm; Pilot_Dia_5=23.56 mm; Pilot_top_1=814.38 mm; Pilot_top_ref=90.63 mm; Profile1_Height=616 mm; Profile1_Length=113.51 mm; Profile1_Length_2=75.68 mm; Profile_Dia=15 mm  [stored 0.0492126 ft]; Profile_Dia_2=15 mm  [stored 0.0492126 ft]; Profile_Dia_3=30 mm  [stored 0.0984252 ft]; Top_Profile=580 mm; Top_Profile_Ref=585 mm; Top_Ref=723.75 mm; Top_Ref_2=769.06 mm; W=1020 mm; W_Ref=1012.5 mm
- 879-0600-00-144002399A0_DN600_PN16: Body_Collar_Dia=151.04 mm; Body_Collar_Dia_2=130.04 mm; Body_Flange_Dia=467.74 mm; Body_Flange_Dia_2=517.86 mm; Body_Height_1=362.5 mm; Body_Height_2=181.25 mm; Body_Height_3=145 mm; Body_Height_4=196.25 mm; Body_Top_Dia=65.02 mm; Body_Top_Dia_2=54.19 mm; Body_With_Dia=362.5 mm; Body_With_Dia_2=391.89 mm; Bolt_support=966.67 mm; Bolt_support_2=483.33 mm; Bolt_support_Dia=30 mm  [stored 0.0984252 ft]; Bolt_support_lenght=320.08 mm; Bolt_support_lenght_2=330.08 mm; Bottom_profile=150.04 mm; D1=360 mm; DN=600.16 mm; FOD=420 mm; Fillet_Length=30 mm  [stored 0.0984252 ft]; Flange_thickness=36 mm  [stored 0.11811 ft]; H3=1325 mm; ID=300.08 mm; L=1450 mm; L1=1467 mm; L_Ref=1458.5 mm; PG_Dia=200.05 mm; PG_Ref=241.67 mm; PG_depth=21 mm  [stored 0.0688976 ft]; PG_ref=310.08 mm; Pilot_Dia_1=106 mm; Pilot_Dia_2=212 mm; Pilot_Dia_3=70.67 mm; Pilot_Dia_4=35.33 mm; Pilot_Dia_5=23.56 mm; Pilot_top_1=814.38 mm; Pilot_top_ref=90.63 mm; Profile1_Height=660 mm; Profile1_Length=113.51 mm; Profile1_Length_2=75.68 mm; Profile_Dia=15 mm  [stored 0.0492126 ft]; Profile_Dia_2=15 mm  [stored 0.0492126 ft]; Profile_Dia_3=30 mm  [stored 0.0984252 ft]; Top_Profile=580 mm; Top_Profile_Ref=585 mm; Top_Ref=723.75 mm; Top_Ref_2=769.06 mm; W=1020 mm; W_Ref=1012.5 mm

note: [stored X ft] marks values corroborated as IEEE doubles in the binary element streams (Revit-internal decimal feet)

## geometry (parser evidence)
native form markers: Sweep x4
no freeform markers — native parametric forms only
